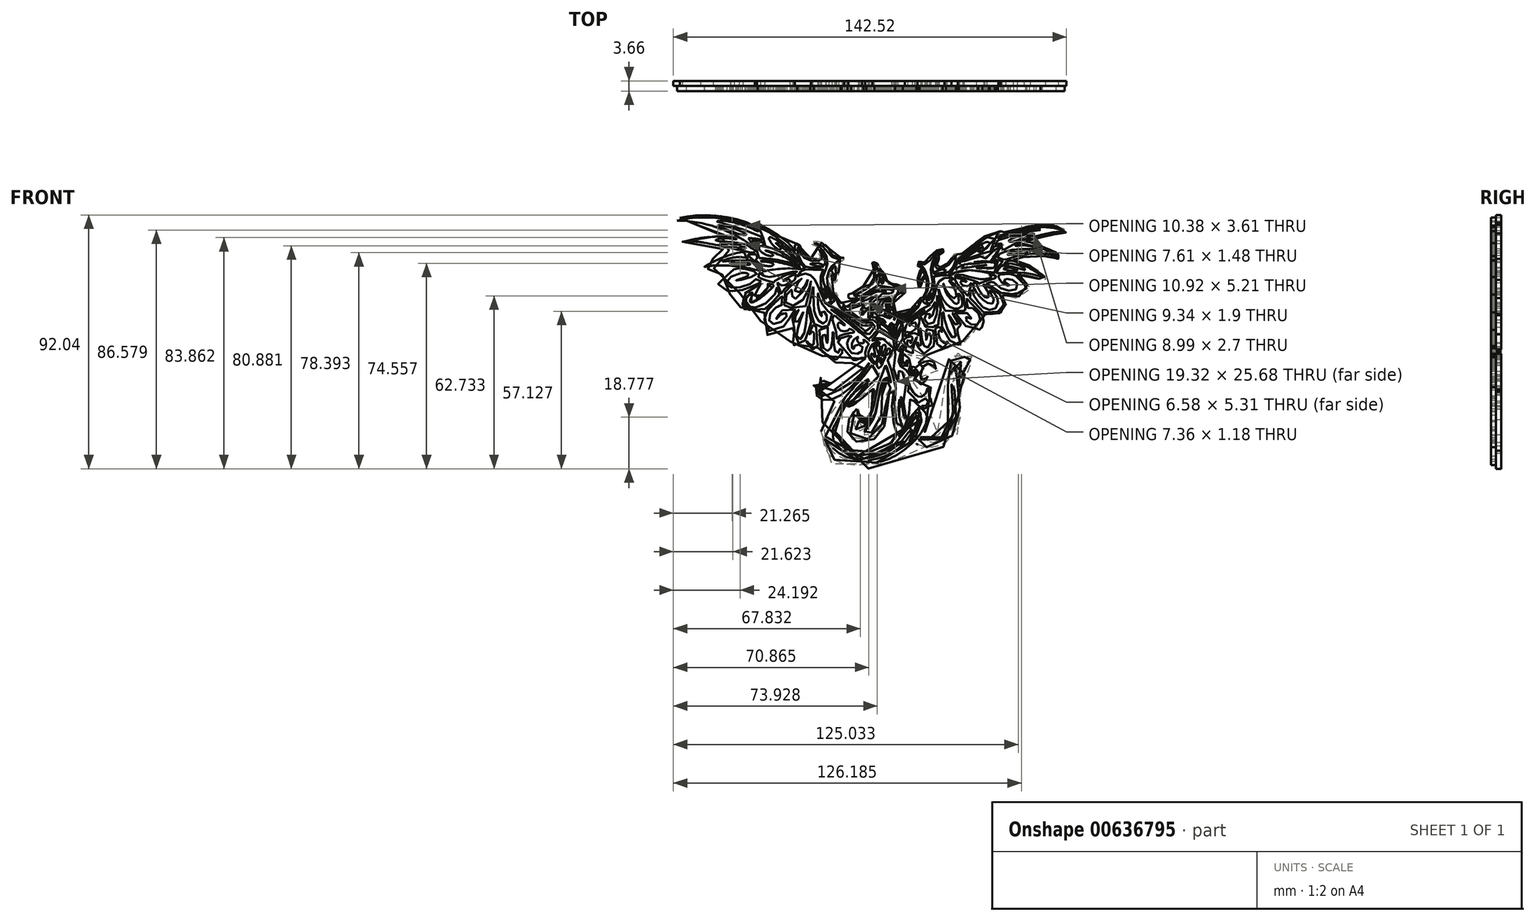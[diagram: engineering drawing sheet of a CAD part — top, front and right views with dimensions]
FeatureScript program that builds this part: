
annotation { "Feature Type Name" : "Feature", "Feature Type Description" : "" }
export const myFeature = defineFeature(function(context is Context, id is Id, definition is map)
    precondition{}
    {
        {
            var Q0;
            Q0=qCreatedBy(makeId("Front.planeOp"),FACE);
            var sketch = newSketch(context, id + "F0", { "sketchPlane" : qUnion([Q0])});
            skArc(sketch, "E0", {"start": v(-40.77, 53.62) * mm, "mid": v(-55.15, 57.82) * mm, "end": v(-70.1, 56.92) * mm});
            skArc(sketch, "E1", {"start": v(-40.6, 52.92) * mm, "mid": v(-40.59, 53.3) * mm, "end": v(-40.77, 53.62) * mm});
            skArc(sketch, "E2", {"start": v(-42.99, 47.81) * mm, "mid": v(-55.82, 54.53) * mm, "end": v(-70.1, 56.92) * mm});
            skArc(sketch, "E3", {"start": v(-42.99, 47.81) * mm, "mid": v(-43.46, 49.24) * mm, "end": v(-44.23, 50.52) * mm});
            skArc(sketch, "E4", {"start": v(-39.37, 49.9) * mm, "mid": v(-41.78, 50.38) * mm, "end": v(-44.23, 50.52) * mm});
            skArc(sketch, "E5", {"start": v(-39.37, 49.9) * mm, "mid": v(-39.28, 49.96) * mm, "end": v(-39.27, 50.07) * mm});
            skArc(sketch, "E6", {"start": v(-39.27, 50.07) * mm, "mid": v(-39.45, 50.65) * mm, "end": v(-39.76, 51.18) * mm});
            skArc(sketch, "E7", {"start": v(-39.76, 51.18) * mm, "mid": v(-47.54, 54.14) * mm, "end": v(-55.52, 56.51) * mm});
            skArc(sketch, "E8", {"start": v(-55.52, 56.73) * mm, "mid": v(-55.53, 56.62) * mm, "end": v(-55.52, 56.51) * mm});
            skArc(sketch, "E9", {"start": v(-50.72, 56.51) * mm, "mid": v(-53.1, 56.86) * mm, "end": v(-55.52, 56.73) * mm});
            skArc(sketch, "E10", {"start": v(-40.6, 52.92) * mm, "mid": v(-45.53, 55.07) * mm, "end": v(-50.72, 56.51) * mm});
            skSolve(sketch);
        }
        {
            var Q0;
            Q0=qCreatedBy(makeId("Front.planeOp"),FACE);
            var sketch = newSketch(context, id + "F1", { "sketchPlane" : qUnion([Q0])});
            skArc(sketch, "E11", {"start": v(-48.78, 52.4) * mm, "mid": v(-47, 51.89) * mm, "end": v(-45.15, 51.67) * mm});
            skArc(sketch, "E12", {"start": v(-45.15, 51.67) * mm, "mid": v(-45, 51.9) * mm, "end": v(-45.13, 52.16) * mm});
            skArc(sketch, "E13", {"start": v(-45.13, 52.16) * mm, "mid": v(-49.74, 54.12) * mm, "end": v(-54.62, 55.26) * mm});
            skArc(sketch, "E14", {"start": v(-54.62, 55.26) * mm, "mid": v(-55, 55.28) * mm, "end": v(-55.38, 55.16) * mm});
            skArc(sketch, "E15", {"start": v(-55.38, 55.16) * mm, "mid": v(-54.86, 54.8) * mm, "end": v(-54.27, 54.56) * mm});
            skArc(sketch, "E16", {"start": v(-54.27, 54.56) * mm, "mid": v(-51.53, 53.48) * mm, "end": v(-48.78, 52.4) * mm});
            skSolve(sketch);
        }
        {
            var Q0;
            Q0=makeQuery(id+"F0.imprint","IMPRINT",FACE,{"disambiguationData":[TD([[makeQuery(id+"F0.imprint","IMPRINT",EDGE,{"derivedFrom":sQuery(id+"F0.wireOp",EDGE,"E0")}),1.0]])]});
            var Q1;
            Q1=makeQuery(id+"F1.imprint","IMPRINT",FACE,{"disambiguationData":[TD([[makeQuery(id+"F1.imprint","IMPRINT",EDGE,{"derivedFrom":sQuery(id+"F1.wireOp",EDGE,"E11")}),1.0]])]});
            extrude(context, id + "F2", {"entities" : qUnion([Q0, Q1]), "depth" : 1.83 * mm, "offsetDistance" : 25.4 * mm});
        }
        {
            var Q0;
            Q0=makeQuery(id+"F1.imprint","IMPRINT",FACE,{"disambiguationData":[TD([[makeQuery(id+"F1.imprint","IMPRINT",EDGE,{"derivedFrom":sQuery(id+"F1.wireOp",EDGE,"E11")}),1.0]])]});
            extrude(context, id + "F3", {"entities" : qUnion([Q0]), "operationType" : NewBodyOperationType.REMOVE, "depth" : 5.46 * mm, "offsetDistance" : 25.4 * mm});
        }
        {
            var Q0;
            Q0=qCreatedBy(makeId("Front.planeOp"),FACE);
            var sketch = newSketch(context, id + "F4", { "sketchPlane" : qUnion([Q0])});
            skArc(sketch, "E17", {"start": v(-38.05, 47.64) * mm, "mid": v(-39.17, 51.49) * mm, "end": v(-40.89, 55.1) * mm});
            skArc(sketch, "E18", {"start": v(-26.6, 41.7) * mm, "mid": v(-32.02, 45.26) * mm, "end": v(-38.05, 47.64) * mm});
            skArc(sketch, "E19", {"start": v(-26.6, 41.7) * mm, "mid": v(-26.54, 41.8) * mm, "end": v(-26.6, 41.9) * mm});
            skArc(sketch, "E20", {"start": v(-26.6, 41.9) * mm, "mid": v(-30.13, 45.65) * mm, "end": v(-34.16, 48.86) * mm});
            skArc(sketch, "E21", {"start": v(-34.16, 48.86) * mm, "mid": v(-34.23, 48.76) * mm, "end": v(-34.2, 48.64) * mm});
            skArc(sketch, "E22", {"start": v(-32.64, 47.14) * mm, "mid": v(-33.36, 47.95) * mm, "end": v(-34.2, 48.64) * mm});
            skArc(sketch, "E23", {"start": v(-32.64, 46.38) * mm, "mid": v(-32.53, 46.76) * mm, "end": v(-32.64, 47.14) * mm});
            skArc(sketch, "E24", {"start": v(-33.49, 46.52) * mm, "mid": v(-33.08, 46.36) * mm, "end": v(-32.64, 46.38) * mm});
            skArc(sketch, "E25", {"start": v(-36.74, 50.34) * mm, "mid": v(-35.42, 48.17) * mm, "end": v(-33.49, 46.52) * mm});
            skArc(sketch, "E26", {"start": v(-36, 50.86) * mm, "mid": v(-36.54, 50.85) * mm, "end": v(-36.74, 50.34) * mm});
            skArc(sketch, "E27", {"start": v(-34.18, 49.92) * mm, "mid": v(-35.07, 50.42) * mm, "end": v(-36, 50.86) * mm});
            skArc(sketch, "E28", {"start": v(-25.33, 41.19) * mm, "mid": v(-29.35, 45.97) * mm, "end": v(-34.18, 49.92) * mm});
            skArc(sketch, "E29", {"start": v(-25.42, 40.9) * mm, "mid": v(-25.34, 41.03) * mm, "end": v(-25.33, 41.19) * mm});
            skArc(sketch, "E30", {"start": v(-26.8, 41.19) * mm, "mid": v(-26.13, 40.93) * mm, "end": v(-25.42, 40.9) * mm});
            skArc(sketch, "E31", {"start": v(-26.8, 41.19) * mm, "mid": v(-32.16, 44.18) * mm, "end": v(-37.97, 46.16) * mm});
            skArc(sketch, "E32", {"start": v(-37.97, 46.16) * mm, "mid": v(-38.03, 46.15) * mm, "end": v(-38.06, 46.1) * mm});
            skArc(sketch, "E33", {"start": v(-38.06, 46.1) * mm, "mid": v(-38.04, 46.03) * mm, "end": v(-37.97, 45.99) * mm});
            skArc(sketch, "E34", {"start": v(-36.61, 45.49) * mm, "mid": v(-37.28, 45.77) * mm, "end": v(-37.97, 45.99) * mm});
            skArc(sketch, "E35", {"start": v(-35.28, 44.44) * mm, "mid": v(-35.84, 45.1) * mm, "end": v(-36.61, 45.49) * mm});
            skArc(sketch, "E36", {"start": v(-35.31, 44.26) * mm, "mid": v(-35.26, 44.34) * mm, "end": v(-35.28, 44.44) * mm});
            skArc(sketch, "E37", {"start": v(-36.88, 44.26) * mm, "mid": v(-36.1, 44.12) * mm, "end": v(-35.31, 44.26) * mm});
            skArc(sketch, "E38", {"start": v(-40.41, 46.57) * mm, "mid": v(-38.87, 45.08) * mm, "end": v(-36.88, 44.26) * mm});
            skArc(sketch, "E39", {"start": v(-38.93, 47.66) * mm, "mid": v(-40, 47.57) * mm, "end": v(-40.41, 46.57) * mm});
            skArc(sketch, "E40", {"start": v(-38.93, 47.66) * mm, "mid": v(-38.85, 48.4) * mm, "end": v(-39.25, 49.04) * mm});
            skArc(sketch, "E41", {"start": v(-39.25, 49.04) * mm, "mid": v(-41.14, 49.54) * mm, "end": v(-43.07, 49.84) * mm});
            skArc(sketch, "E42", {"start": v(-40.41, 43.35) * mm, "mid": v(-41.47, 46.7) * mm, "end": v(-43.07, 49.84) * mm});
            skArc(sketch, "E43", {"start": v(-26.8, 40.9) * mm, "mid": v(-33.51, 42.63) * mm, "end": v(-40.41, 43.35) * mm});
            skArc(sketch, "E44", {"start": v(-25.65, 40.14) * mm, "mid": v(-26.14, 40.64) * mm, "end": v(-26.8, 40.9) * mm});
            skArc(sketch, "E45", {"start": v(-25.72, 39.85) * mm, "mid": v(-25.64, 39.98) * mm, "end": v(-25.65, 40.14) * mm});
            skArc(sketch, "E46", {"start": v(-27.02, 40.14) * mm, "mid": v(-26.38, 39.95) * mm, "end": v(-25.72, 39.85) * mm});
            skArc(sketch, "E47", {"start": v(-27.02, 40.14) * mm, "mid": v(-30.32, 41.12) * mm, "end": v(-33.67, 41.9) * mm});
            skArc(sketch, "E48", {"start": v(-33.67, 41.9) * mm, "mid": v(-36.75, 42.4) * mm, "end": v(-39.88, 42.32) * mm});
            skArc(sketch, "E49", {"start": v(-39.33, 42) * mm, "mid": v(-39.6, 42.18) * mm, "end": v(-39.88, 42.32) * mm});
            skArc(sketch, "E50", {"start": v(-37.02, 41.9) * mm, "mid": v(-38.17, 42.04) * mm, "end": v(-39.33, 42) * mm});
            skArc(sketch, "E51", {"start": v(-35.1, 41.14) * mm, "mid": v(-36, 41.65) * mm, "end": v(-37.02, 41.9) * mm});
            skArc(sketch, "E52", {"start": v(-35.93, 40.46) * mm, "mid": v(-35.4, 40.67) * mm, "end": v(-35.1, 41.14) * mm});
            skArc(sketch, "E53", {"start": v(-38.64, 40.64) * mm, "mid": v(-37.3, 40.45) * mm, "end": v(-35.93, 40.46) * mm});
            skArc(sketch, "E54", {"start": v(-41.35, 42.49) * mm, "mid": v(-40.15, 41.33) * mm, "end": v(-38.64, 40.64) * mm});
            skArc(sketch, "E55", {"start": v(-41.1, 43.17) * mm, "mid": v(-41.46, 42.91) * mm, "end": v(-41.35, 42.49) * mm});
            skArc(sketch, "E56", {"start": v(-41.1, 43.17) * mm, "mid": v(-41.06, 43.2) * mm, "end": v(-41.03, 43.23) * mm});
            skArc(sketch, "E57", {"start": v(-41.03, 43.23) * mm, "mid": v(-41.18, 43.99) * mm, "end": v(-41.53, 44.67) * mm});
            skArc(sketch, "E58", {"start": v(-41.53, 44.67) * mm, "mid": v(-42.78, 44.77) * mm, "end": v(-44.02, 44.67) * mm});
            skArc(sketch, "E59", {"start": v(-44.02, 44.67) * mm, "mid": v(-44.23, 44.57) * mm, "end": v(-44.38, 44.38) * mm});
            skArc(sketch, "E60", {"start": v(-38.75, 38.5) * mm, "mid": v(-41.42, 41.58) * mm, "end": v(-44.38, 44.38) * mm});
            skArc(sketch, "E61", {"start": v(-26.95, 39.5) * mm, "mid": v(-32.89, 39.43) * mm, "end": v(-38.75, 38.5) * mm});
            skArc(sketch, "E62", {"start": v(-24.8, 39.3) * mm, "mid": v(-25.87, 39.4) * mm, "end": v(-26.95, 39.5) * mm});
            skArc(sketch, "E63", {"start": v(-24.19, 39.5) * mm, "mid": v(-24.51, 39.46) * mm, "end": v(-24.8, 39.3) * mm});
            skArc(sketch, "E64", {"start": v(-24.19, 39.5) * mm, "mid": v(-23.87, 39.64) * mm, "end": v(-23.58, 39.83) * mm});
            skArc(sketch, "E65", {"start": v(-23.82, 39.92) * mm, "mid": v(-23.7, 39.86) * mm, "end": v(-23.58, 39.83) * mm});
            skArc(sketch, "E66", {"start": v(-26.4, 44.25) * mm, "mid": v(-25.49, 41.86) * mm, "end": v(-23.82, 39.92) * mm});
            skArc(sketch, "E67", {"start": v(-26.4, 44.25) * mm, "mid": v(-33.23, 50.24) * mm, "end": v(-40.89, 55.1) * mm});
            skSolve(sketch);
        }
        {
            var Q0;
            Q0=makeQuery(id+"F4.imprint","IMPRINT",FACE,{"disambiguationData":[TD([[makeQuery(id+"F4.imprint","IMPRINT",EDGE,{"derivedFrom":sQuery(id+"F4.wireOp",EDGE,"E17")}),-1.0]])]});
            extrude(context, id + "F5", {"entities" : qUnion([Q0]), "depth" : 1.83 * mm, "offsetDistance" : 25.4 * mm});
        }
        {
            var Q0;
            Q0=qCreatedBy(makeId("Front.planeOp"),FACE);
            var sketch = newSketch(context, id + "F6", { "sketchPlane" : qUnion([Q0])});
            skArc(sketch, "E68", {"start": v(-49.84, 50.91) * mm, "mid": v(-58.28, 50.99) * mm, "end": v(-66.62, 49.6) * mm});
            skArc(sketch, "E69", {"start": v(-48.6, 50.33) * mm, "mid": v(-49.21, 50.64) * mm, "end": v(-49.84, 50.91) * mm});
            skArc(sketch, "E70", {"start": v(-48.57, 50.12) * mm, "mid": v(-48.52, 50.24) * mm, "end": v(-48.6, 50.33) * mm});
            skArc(sketch, "E71", {"start": v(-49.67, 50.33) * mm, "mid": v(-49.13, 50.18) * mm, "end": v(-48.57, 50.12) * mm});
            skArc(sketch, "E72", {"start": v(-49.67, 50.33) * mm, "mid": v(-51.75, 50.52) * mm, "end": v(-53.83, 50.48) * mm});
            skArc(sketch, "E73", {"start": v(-53.83, 50.48) * mm, "mid": v(-55, 50.32) * mm, "end": v(-56.12, 49.87) * mm});
            skArc(sketch, "E74", {"start": v(-56.12, 49.87) * mm, "mid": v(-55.84, 49.73) * mm, "end": v(-55.54, 49.65) * mm});
            skArc(sketch, "E75", {"start": v(-55.54, 49.65) * mm, "mid": v(-54.6, 49.45) * mm, "end": v(-53.63, 49.31) * mm});
            skArc(sketch, "E76", {"start": v(-45.04, 48.31) * mm, "mid": v(-49.31, 49) * mm, "end": v(-53.63, 49.31) * mm});
            skArc(sketch, "E77", {"start": v(-45.04, 48.31) * mm, "mid": v(-43.73, 47.36) * mm, "end": v(-42.36, 46.5) * mm});
            skArc(sketch, "E78", {"start": v(-41.82, 45.43) * mm, "mid": v(-41.95, 46.03) * mm, "end": v(-42.36, 46.5) * mm});
            skArc(sketch, "E79", {"start": v(-44, 45.43) * mm, "mid": v(-42.91, 45.36) * mm, "end": v(-41.82, 45.43) * mm});
            skArc(sketch, "E80", {"start": v(-44, 45.43) * mm, "mid": v(-52.12, 47.34) * mm, "end": v(-60.3, 48.96) * mm});
            skArc(sketch, "E81", {"start": v(-60.3, 48.96) * mm, "mid": v(-63.45, 49.4) * mm, "end": v(-66.62, 49.6) * mm});
            skSolve(sketch);
        }
        {
            var Q0;
            Q0=qCreatedBy(makeId("Front.planeOp"),FACE);
            var sketch = newSketch(context, id + "F7", { "sketchPlane" : qUnion([Q0])});
            skArc(sketch, "E82", {"start": v(-54.5, 48.54) * mm, "mid": v(-54.44, 48.45) * mm, "end": v(-54.33, 48.4) * mm});
            skArc(sketch, "E83", {"start": v(-54.17, 48.72) * mm, "mid": v(-54.37, 48.7) * mm, "end": v(-54.5, 48.54) * mm});
            skArc(sketch, "E84", {"start": v(-45.2, 47.13) * mm, "mid": v(-49.6, 48.36) * mm, "end": v(-54.17, 48.72) * mm});
            skArc(sketch, "E85", {"start": v(-45.2, 46.91) * mm, "mid": v(-45.16, 47.02) * mm, "end": v(-45.2, 47.13) * mm});
            skArc(sketch, "E86", {"start": v(-45.74, 46.83) * mm, "mid": v(-45.46, 46.85) * mm, "end": v(-45.2, 46.91) * mm});
            skArc(sketch, "E87", {"start": v(-54.33, 48.4) * mm, "mid": v(-50.08, 47.36) * mm, "end": v(-45.74, 46.83) * mm});
            skSolve(sketch);
        }
        {
            var Q0;
            Q0=makeQuery(id+"F6.imprint","IMPRINT",FACE,{"disambiguationData":[TD([[makeQuery(id+"F6.imprint","IMPRINT",EDGE,{"derivedFrom":sQuery(id+"F6.wireOp",EDGE,"E68")}),1.0]])]});
            extrude(context, id + "F8", {"entities" : qUnion([Q0]), "depth" : 1.83 * mm, "offsetDistance" : 25.4 * mm});
        }
        {
            var Q0;
            Q0=makeQuery(id+"F7.imprint","IMPRINT",FACE,{"disambiguationData":[TD([[makeQuery(id+"F7.imprint","IMPRINT",EDGE,{"derivedFrom":sQuery(id+"F7.wireOp",EDGE,"E82")}),1.0]])]});
            extrude(context, id + "F9", {"entities" : qUnion([Q0]), "operationType" : NewBodyOperationType.REMOVE, "depth" : 12.2 * mm, "offsetDistance" : 25.4 * mm});
        }
        {
            var Q0;
            Q0=qCreatedBy(makeId("Front.planeOp"),FACE);
            var sketch = newSketch(context, id + "F10", { "sketchPlane" : qUnion([Q0])});
            skArc(sketch, "E88", {"start": v(-45.43, 44.47) * mm, "mid": v(-44.95, 43.94) * mm, "end": v(-44.4, 43.47) * mm});
            skArc(sketch, "E89", {"start": v(-45.43, 45.01) * mm, "mid": v(-45.47, 44.74) * mm, "end": v(-45.43, 44.47) * mm});
            skArc(sketch, "E90", {"start": v(-45.43, 45.01) * mm, "mid": v(-45.95, 45.32) * mm, "end": v(-46.5, 45.54) * mm});
            skArc(sketch, "E91", {"start": v(-46.5, 45.54) * mm, "mid": v(-53.55, 43.56) * mm, "end": v(-60.08, 40.25) * mm});
            skArc(sketch, "E92", {"start": v(-60.08, 40.25) * mm, "mid": v(-60.1, 40.19) * mm, "end": v(-60.05, 40.16) * mm});
            skArc(sketch, "E93", {"start": v(-55.05, 40.67) * mm, "mid": v(-57.56, 40.58) * mm, "end": v(-60.05, 40.16) * mm});
            skArc(sketch, "E94", {"start": v(-40, 38.68) * mm, "mid": v(-47.45, 40.24) * mm, "end": v(-55.05, 40.67) * mm});
            skArc(sketch, "E95", {"start": v(-40, 38.68) * mm, "mid": v(-39.91, 38.72) * mm, "end": v(-39.86, 38.8) * mm});
            skArc(sketch, "E96", {"start": v(-39.86, 38.8) * mm, "mid": v(-41.59, 40.7) * mm, "end": v(-43.42, 42.5) * mm});
            skArc(sketch, "E97", {"start": v(-53.36, 42.4) * mm, "mid": v(-53.5, 42.28) * mm, "end": v(-53.43, 42.1) * mm});
            skArc(sketch, "E98", {"start": v(-44.47, 43.28) * mm, "mid": v(-49, 43.62) * mm, "end": v(-53.36, 42.4) * mm});
            skArc(sketch, "E99", {"start": v(-44.47, 43.28) * mm, "mid": v(-44.38, 43.35) * mm, "end": v(-44.4, 43.47) * mm});
            skArc(sketch, "E100", {"start": v(-48.28, 42.4) * mm, "mid": v(-50.86, 42.34) * mm, "end": v(-53.43, 42.1) * mm});
            skArc(sketch, "E101", {"start": v(-43.42, 42.5) * mm, "mid": v(-45.85, 42.48) * mm, "end": v(-48.28, 42.4) * mm});
            skSolve(sketch);
        }
        {
            var Q0;
            Q0=makeQuery(id+"F10.imprint","IMPRINT",FACE,{"disambiguationData":[TD([[makeQuery(id+"F10.imprint","IMPRINT",EDGE,{"derivedFrom":sQuery(id+"F10.wireOp",EDGE,"E88")}),-1.0]])]});
            extrude(context, id + "F11", {"entities" : qUnion([Q0]), "depth" : 1.83 * mm, "offsetDistance" : 25.4 * mm});
        }
        {
            var Q0;
            Q0=qCreatedBy(makeId("Front.planeOp"),FACE);
            var sketch = newSketch(context, id + "F12", { "sketchPlane" : qUnion([Q0])});
            skArc(sketch, "E102", {"start": v(-50.87, 41.4) * mm, "mid": v(-50.6, 41.3) * mm, "end": v(-50.33, 41.26) * mm});
            skArc(sketch, "E103", {"start": v(-50.87, 41.62) * mm, "mid": v(-50.94, 41.51) * mm, "end": v(-50.87, 41.4) * mm});
            skArc(sketch, "E104", {"start": v(-43.7, 41.4) * mm, "mid": v(-47.27, 42.05) * mm, "end": v(-50.87, 41.62) * mm});
            skArc(sketch, "E105", {"start": v(-43.7, 40.96) * mm, "mid": v(-43.58, 41.18) * mm, "end": v(-43.7, 41.4) * mm});
            skArc(sketch, "E106", {"start": v(-50.33, 41.26) * mm, "mid": v(-47.02, 40.89) * mm, "end": v(-43.7, 40.96) * mm});
            skSolve(sketch);
        }
        {
            var Q0;
            Q0 = qSketchRegion(id + "F12", true);
            extrude(context, id + "F13", {"entities" : qUnion([Q0]), "operationType" : NewBodyOperationType.REMOVE, "depth" : 25.4 * mm, "offsetDistance" : 25.4 * mm});
        }
        {
            var Q0;
            Q0=qCreatedBy(makeId("Front.planeOp"),FACE);
            var sketch = newSketch(context, id + "F14", { "sketchPlane" : qUnion([Q0])});
            skArc(sketch, "E107", {"start": v(-48.7, 35.2) * mm, "mid": v(-48.64, 35.18) * mm, "end": v(-48.57, 35.2) * mm});
            skArc(sketch, "E108", {"start": v(-48.7, 35.32) * mm, "mid": v(-48.72, 35.26) * mm, "end": v(-48.7, 35.2) * mm});
            skArc(sketch, "E109", {"start": v(-48.7, 35.32) * mm, "mid": v(-48.24, 35.44) * mm, "end": v(-47.78, 35.58) * mm});
            skFitSpline(sketch, "E110", {"points": [v(-47.78, 35.58) * mm, v(-44.29, 37.27) * mm, v(-44.4, 37.7) * mm, v(-44.4, 37.67) * mm, v(-44.4, 37.68) * mm], "startDerivative": vector(7.46, 2.33) * mm, "endDerivative": vector(0.28, 0.45) * mm});
            skArc(sketch, "E111", {"start": v(-44.4, 37.68) * mm, "mid": v(-45.74, 38) * mm, "end": v(-47.11, 37.88) * mm});
            skFitSpline(sketch, "E112", {"points": [v(-47.11, 37.88) * mm, v(-50.57, 36.51) * mm, v(-51.69, 35.46) * mm, v(-51.95, 34.74) * mm, v(-51.96, 33.96) * mm, v(-51.61, 33.32) * mm, v(-51.11, 32.92) * mm, v(-50.54, 32.69) * mm, v(-48.43, 32.65) * mm, v(-45.08, 33.38) * mm, v(-41.98, 35.07) * mm, v(-41.38, 35.78) * mm, v(-41, 35.53) * mm, v(-39.63, 34.88) * mm, v(-39.67, 34.77) * mm, v(-39.93, 34.52) * mm, v(-40.7, 34.13) * mm, v(-42.68, 33.16) * mm, v(-45.8, 31.94) * mm, v(-49.7, 31.38) * mm, v(-51.04, 31.18) * mm, v(-51.23, 31.16) * mm, v(-55.08, 33.82) * mm, v(-55.12, 34.1) * mm, v(-53.64, 35.58) * mm, v(-49.26, 39.54) * mm, v(-49.16, 39.59) * mm, v(-47.93, 39.6) * mm, v(-45.95, 39.44) * mm, v(-44.31, 39.2) * mm, v(-41.57, 38.5) * mm, v(-41.23, 38.42) * mm, v(-41.2, 37.5) * mm, v(-41.22, 37.38) * mm, v(-44.02, 36.24) * mm, v(-47.05, 35.45) * mm, v(-48.18, 35.24) * mm, v(-48.57, 35.2) * mm], "startDerivative": vector(-88.5, -28.85) * mm, "endDerivative": vector(-24.4, -1.68) * mm});
            skSolve(sketch);
        }
        {
            var Q0;
            Q0 = qSketchRegion(id + "F14", true);
            extrude(context, id + "F15", {"entities" : qUnion([Q0]), "depth" : 1.83 * mm, "offsetDistance" : 25.4 * mm});
        }
        {
            var Q0;
            Q0=qCreatedBy(makeId("Front.planeOp"),FACE);
            var sketch = newSketch(context, id + "F16", { "sketchPlane" : qUnion([Q0])});
            skFitSpline(sketch, "E113", {"points": [v(-38.89, 37.85) * mm, v(-39.35, 37.62) * mm, v(-39.47, 37.4) * mm, v(-39.34, 37.2) * mm, v(-38.84, 36.95) * mm, v(-37.39, 36.55) * mm, v(-35.11, 36.71) * mm, v(-27.73, 38.42) * mm, v(-26.95, 38.5) * mm, v(-26.59, 38.5) * mm, v(-26.58, 38.44) * mm, v(-27.4, 38.17) * mm, v(-29.43, 37.54) * mm, v(-30.77, 37.1) * mm, v(-32.37, 36.3) * mm, v(-34.38, 35.16) * mm, v(-34.94, 34.68) * mm, v(-35.02, 34.56) * mm, v(-35.02, 34.54) * mm, v(-37.35, 35.15) * mm, v(-39.65, 35.95) * mm, v(-40.42, 36.37) * mm, v(-40.54, 36.46) * mm, v(-40.48, 37.04) * mm, v(-40.2, 37.9) * mm, v(-40.14, 37.92) * mm, v(-38.89, 37.85) * mm]});
            skSolve(sketch);
        }
        {
            var Q0;
            Q0 = qSketchRegion(id + "F16", true);
            extrude(context, id + "F17", {"entities" : qUnion([Q0]), "depth" : 1.83 * mm, "offsetDistance" : 25.4 * mm});
        }
        {
            var Q0;
            Q0=qCreatedBy(makeId("Front.planeOp"),FACE);
            var sketch = newSketch(context, id + "F18", { "sketchPlane" : qUnion([Q0])});
            skFitSpline(sketch, "E114", {"points": [v(-37.05, 34) * mm, v(-35.03, 33.59) * mm, v(-34.99, 33.38) * mm, v(-35.23, 33.01) * mm, v(-37.45, 30.91) * mm, v(-39.33, 29.33) * mm, v(-41.86, 27.66) * mm, v(-42.67, 27.26) * mm, v(-43.28, 27.22) * mm, v(-43.5, 27.37) * mm, v(-43.62, 27.76) * mm, v(-43.53, 28.21) * mm, v(-43.05, 29.24) * mm, v(-42.64, 30.16) * mm, v(-42.61, 30.64) * mm, v(-42.72, 30.83) * mm, v(-43, 30.86) * mm, v(-43.57, 30.65) * mm, v(-44.27, 29.9) * mm, v(-44.82, 29.06) * mm, v(-45.2, 28.19) * mm, v(-45.3, 26.85) * mm, v(-45.24, 26.23) * mm, v(-44.64, 25.69) * mm, v(-43.48, 25.49) * mm, v(-42.32, 25.43) * mm, v(-40.6, 25.59) * mm, v(-39.3, 26.11) * mm, v(-37.42, 27.29) * mm, v(-35.58, 29) * mm, v(-34.3, 30.72) * mm, v(-34, 31.6) * mm, v(-33.93, 32.14) * mm, v(-33.91, 32.52) * mm, v(-33.88, 32.67) * mm, v(-33.7, 32.68) * mm, v(-33.67, 32.3) * mm, v(-33.13, 30.49) * mm, v(-32.95, 30.2) * mm, v(-33.04, 29.8) * mm, v(-34.06, 28.77) * mm, v(-35.82, 27.01) * mm, v(-37.4, 25.66) * mm, v(-38.23, 24.86) * mm, v(-38.36, 24.78) * mm, v(-41.4, 24.83) * mm, v(-45.28, 24.41) * mm, v(-45.5, 24.56) * mm, v(-45.75, 25.1) * mm, v(-46.36, 26.59) * mm, v(-46.23, 27.21) * mm, v(-45.05, 31.22) * mm, v(-44.69, 31.4) * mm, v(-39.04, 34.23) * mm, v(-39.03, 34.03) * mm, v(-39.68, 33.48) * mm, v(-40.65, 32.28) * mm, v(-41.43, 31.1) * mm, v(-41.83, 30.2) * mm, v(-41.96, 29.8) * mm, v(-41.9, 29.23) * mm, v(-41.64, 29.03) * mm, v(-41.1, 29.07) * mm, v(-39.93, 29.79) * mm, v(-38.6, 30.88) * mm, v(-37.4, 32.27) * mm, v(-37.14, 32.7) * mm, v(-37.1, 33.09) * mm, v(-37.13, 33.43) * mm, v(-37.2, 33.78) * mm, v(-37.21, 33.93) * mm, v(-37.05, 34) * mm]});
            skSolve(sketch);
        }
        {
            var Q0;
            Q0 = qSketchRegion(id + "F18", true);
            extrude(context, id + "F19", {"entities" : qUnion([Q0]), "depth" : 1.83 * mm, "offsetDistance" : 25.4 * mm});
        }
        {
            var Q0;
            Q0=qCreatedBy(makeId("Front.planeOp"),FACE);
            var sketch = newSketch(context, id + "F20", { "sketchPlane" : qUnion([Q0])});
            skFitSpline(sketch, "E115", {"points": [v(-33.68, 34.55) * mm, v(-33.38, 34.27) * mm, v(-33.02, 33.77) * mm, v(-32.31, 33.41) * mm, v(-31.52, 33.34) * mm, v(-30.11, 33.91) * mm, v(-29.43, 34.46) * mm, v(-29.03, 35.15) * mm, v(-29.15, 35.62) * mm, v(-29.75, 35.69) * mm, v(-30.86, 35.42) * mm, v(-31.25, 35.16) * mm, v(-31.56, 34.99) * mm, v(-31.65, 34.99) * mm, v(-31.69, 35.2) * mm, v(-31.31, 35.47) * mm, v(-30.13, 36.17) * mm, v(-27.53, 37.32) * mm, v(-26.93, 37.53) * mm, v(-26.81, 37.46) * mm, v(-26.89, 37.36) * mm, v(-27.07, 36.84) * mm, v(-27.14, 36.47) * mm, v(-27.06, 35.9) * mm, v(-27.36, 35.55) * mm, v(-28.87, 34.23) * mm, v(-30.11, 33.08) * mm, v(-31.57, 31.5) * mm, v(-32.17, 30.6) * mm, v(-32.33, 30.4) * mm, v(-32.41, 30.44) * mm, v(-32.4, 30.63) * mm, v(-33.46, 33.38) * mm, v(-33.72, 34.17) * mm, v(-33.76, 34.43) * mm, v(-33.68, 34.55) * mm]});
            skSolve(sketch);
        }
        {
            var Q0;
            Q0 = qSketchRegion(id + "F20", true);
            extrude(context, id + "F21", {"entities" : qUnion([Q0]), "depth" : 1.83 * mm, "offsetDistance" : 25.4 * mm});
        }
        {
            var Q0;
            Q0=qCreatedBy(makeId("Front.planeOp"),FACE);
            var sketch = newSketch(context, id + "F22", { "sketchPlane" : qUnion([Q0])});
            skFitSpline(sketch, "E116", {"points": [v(-22.68, 35.58) * mm, v(-22.56, 35.69) * mm, v(-22.54, 35.37) * mm, v(-22.74, 34.55) * mm, v(-23.33, 33.16) * mm, v(-24.09, 31.83) * mm, v(-25.43, 30.2) * mm, v(-26.5, 29.12) * mm, v(-27.6, 28.37) * mm, v(-28.51, 28.4) * mm, v(-28.42, 29.12) * mm, v(-28.2, 30.63) * mm, v(-28.2, 31.6) * mm, v(-28.59, 31.88) * mm, v(-29.7, 31.48) * mm, v(-30.4, 30.38) * mm, v(-30.69, 29.19) * mm, v(-30.8, 28.05) * mm, v(-30.56, 27.03) * mm, v(-29.46, 26.17) * mm, v(-27.83, 26.1) * mm, v(-25.4, 27.32) * mm, v(-23.35, 29.84) * mm, v(-22, 32.77) * mm, v(-21.74, 34.33) * mm, v(-21.66, 34.88) * mm, v(-21.55, 34.88) * mm, v(-21.52, 34) * mm, v(-21.9, 31.87) * mm, v(-23.5, 26) * mm, v(-23.5, 25.96) * mm, v(-25.24, 25.84) * mm, v(-30.72, 25.2) * mm, v(-31.07, 25.46) * mm, v(-31.18, 26.72) * mm, v(-31.07, 30.88) * mm, v(-30.97, 31) * mm, v(-30.2, 31.92) * mm, v(-28.8, 33.23) * mm, v(-25.52, 35.6) * mm, v(-24.83, 35.86) * mm, v(-24.74, 35.69) * mm, v(-25.28, 35.34) * mm, v(-26.4, 34.25) * mm, v(-27.23, 32.84) * mm, v(-27.42, 31.49) * mm, v(-27.18, 30.66) * mm, v(-26.37, 30.66) * mm, v(-25.45, 31.21) * mm, v(-24.16, 32.63) * mm, v(-23.36, 33.9) * mm, v(-22.82, 34.95) * mm, v(-22.75, 35.36) * mm, v(-22.68, 35.58) * mm]});
            skSolve(sketch);
        }
        {
            var Q0;
            Q0=makeQuery(id+"F22.imprint","IMPRINT",FACE,{"disambiguationData":[TD([[makeQuery(id+"F22.imprint","IMPRINT",EDGE,{"derivedFrom":sQuery(id+"F22.wireOp",EDGE,"E116")}),-1.0]])]});
            extrude(context, id + "F23", {"entities" : qUnion([Q0]), "depth" : 1.83 * mm, "offsetDistance" : 25.4 * mm});
        }
        {
            var Q0;
            Q0=qCreatedBy(makeId("Front.planeOp"),FACE);
            var sketch = newSketch(context, id + "F24", { "sketchPlane" : qUnion([Q0])});
            skFitSpline(sketch, "E117", {"points": [v(-31.92, 24.4) * mm, v(-27.33, 24.7) * mm, v(-27.31, 24.6) * mm, v(-27.89, 23.67) * mm, v(-31.09, 18.91) * mm, v(-31.43, 18.52) * mm, v(-31.95, 18.41) * mm, v(-33.82, 17.8) * mm, v(-35.26, 17.33) * mm, v(-36.86, 16.8) * mm, v(-36.87, 16.8) * mm, v(-37.34, 18.3) * mm, v(-37.89, 19.88) * mm, v(-38.35, 20.84) * mm, v(-38.45, 21.22) * mm, v(-38.28, 21.85) * mm, v(-37.2, 24.77) * mm, v(-37.16, 24.83) * mm, v(-33.76, 27.88) * mm, v(-32.88, 28.78) * mm, v(-32.34, 29.44) * mm, v(-32.17, 29.62) * mm, v(-31.94, 29.68) * mm, v(-31.9, 29.56) * mm, v(-32.03, 26.42) * mm, v(-32.03, 26.34) * mm, v(-32.7, 26.3) * mm, v(-33.48, 25.92) * mm, v(-34.53, 25.25) * mm, v(-35.93, 23.87) * mm, v(-36.76, 22.3) * mm, v(-36.73, 20.81) * mm, v(-36.34, 20.04) * mm, v(-35.68, 19.57) * mm, v(-34.41, 19.52) * mm, v(-32.71, 20.09) * mm, v(-31.1, 21.17) * mm, v(-30.4, 22.1) * mm, v(-30.2, 22.68) * mm, v(-30.24, 23.14) * mm, v(-30.56, 23.37) * mm, v(-31.16, 23.36) * mm, v(-31.96, 23.12) * mm, v(-32.89, 22.57) * mm, v(-33.72, 21.74) * mm, v(-34.12, 21.26) * mm, v(-34.16, 21.3) * mm, v(-34.17, 21.5) * mm, v(-33.88, 21.9) * mm, v(-32.13, 24.11) * mm, v(-31.98, 24.3) * mm, v(-31.95, 24.36) * mm, v(-31.94, 24.37) * mm, v(-31.93, 24.39) * mm, v(-31.92, 24.39) * mm, v(-31.92, 24.4) * mm, v(-31.92, 24.4) * mm, v(-31.92, 24.4) * mm]});
            skSolve(sketch);
        }
        {
            var Q0;
            Q0=makeQuery(id+"F24.imprint","IMPRINT",FACE,{"disambiguationData":[TD([[makeQuery(id+"F24.imprint","IMPRINT",EDGE,{"derivedFrom":sQuery(id+"F24.wireOp",EDGE,"E117")}),-1.0]])]});
            extrude(context, id + "F25", {"entities" : qUnion([Q0]), "depth" : 1.83 * mm, "offsetDistance" : 25.4 * mm});
        }
        {
            var Q0;
            Q0=qCreatedBy(makeId("Front.planeOp"),FACE);
            var sketch = newSketch(context, id + "F26", { "sketchPlane" : qUnion([Q0])});
            skFitSpline(sketch, "E118", {"points": [v(-20.63, 32.94) * mm, v(-20.64, 30.1) * mm, v(-20.57, 26.68) * mm, v(-20.33, 24.05) * mm, v(-19.88, 22.65) * mm, v(-19.44, 21.58) * mm, v(-18.5, 20.21) * mm, v(-17.21, 19.57) * mm, v(-16.26, 20.12) * mm, v(-15.78, 20.97) * mm, v(-15.76, 22.11) * mm, v(-16.2, 23.22) * mm, v(-16.7, 23.91) * mm, v(-17.4, 24.13) * mm, v(-17.82, 23.62) * mm, v(-17.83, 22.92) * mm, v(-17.64, 22.2) * mm, v(-17.66, 21.94) * mm, v(-17.85, 22.13) * mm, v(-18.3, 23.29) * mm, v(-18.64, 24.33) * mm, v(-18.85, 25.26) * mm, v(-19.07, 27.83) * mm, v(-19.1, 29.68) * mm, v(-19.15, 30.44) * mm, v(-18.93, 30.54) * mm, v(-18.78, 29.9) * mm, v(-18.12, 27.8) * mm, v(-16.8, 25.7) * mm, v(-14.6, 23.4) * mm, v(-14.01, 23.01) * mm, v(-14.01, 22.8) * mm, v(-14.36, 21.6) * mm, v(-15.38, 18.95) * mm, v(-15.43, 18.83) * mm, v(-17.68, 18.27) * mm], "startDerivative": vector(-0.75, -62.98) * mm, "endDerivative": vector(-78.97, -16.88) * mm});
            skFitSpline(sketch, "E119", {"points": [v(-17.68, 18.27) * mm, v(-20.25, 19.49) * mm, v(-20.4, 19.59) * mm, v(-21.64, 24.11) * mm, v(-21.9, 25.28) * mm, v(-22.28, 26.1) * mm, v(-22.15, 26.6) * mm, v(-21.94, 27.3) * mm, v(-21.44, 29.8) * mm, v(-21.17, 30.98) * mm, v(-20.8, 32.68) * mm, v(-20.72, 32.85) * mm, v(-20.63, 32.94) * mm], "startDerivative": vector(-25.53, 12.8) * mm, "endDerivative": vector(3.47, 3.11) * mm});
            skSolve(sketch);
        }
        {
            var Q0;
            Q0 = qSketchRegion(id + "F26", true);
            extrude(context, id + "F27", {"entities" : qUnion([Q0]), "depth" : 1.83 * mm, "offsetDistance" : 25.4 * mm});
        }
        {
            var Q0;
            Q0=qCreatedBy(makeId("Front.planeOp"),FACE);
            var sketch = newSketch(context, id + "F28", { "sketchPlane" : qUnion([Q0])});
            skFitSpline(sketch, "E120", {"points": [v(-22.63, 25.6) * mm, v(-21.41, 20.15) * mm, v(-21.4, 20) * mm, v(-21.92, 18.34) * mm, v(-23.65, 13.63) * mm, v(-23.72, 13.46) * mm, v(-27.31, 11.9) * mm, v(-28.17, 11.52) * mm, v(-28.22, 11.64) * mm, v(-28.05, 12.82) * mm, v(-27.67, 16.25) * mm, v(-27.4, 18.69) * mm, v(-27.5, 18.87) * mm, v(-28.34, 20.36) * mm, v(-28.58, 20.95) * mm, v(-28.47, 21.15) * mm, v(-27.59, 22.44) * mm, v(-26.99, 23.47) * mm, v(-26.45, 24.35) * mm, v(-26.12, 24.74) * mm, v(-25.96, 24.74) * mm, v(-26.14, 24.47) * mm, v(-26.75, 23.3) * mm, v(-27.25, 22.18) * mm, v(-27.52, 21.08) * mm, v(-27.54, 20.51) * mm, v(-27.09, 19.9) * mm, v(-26.55, 19.95) * mm, v(-26.16, 20.38) * mm, v(-25.31, 21.82) * mm, v(-24.7, 23.15) * mm, v(-24.38, 23.9) * mm, v(-24.28, 24.02) * mm, v(-24.23, 24) * mm, v(-24.4, 23.36) * mm, v(-25.12, 21.54) * mm, v(-25.57, 20.32) * mm, v(-26.2, 18.37) * mm, v(-26.62, 16.26) * mm, v(-26.72, 15.24) * mm, v(-26.48, 14.36) * mm, v(-25.77, 13.93) * mm, v(-24.89, 14.2) * mm, v(-24.13, 15.54) * mm, v(-23.75, 17.07) * mm, v(-23.28, 20.25) * mm, v(-23.02, 23.37) * mm, v(-22.85, 25.38) * mm, v(-22.8, 25.53) * mm, v(-22.72, 25.57) * mm, v(-22.63, 25.6) * mm]});
            skSolve(sketch);
        }
        {
            var Q0;
            Q0 = qSketchRegion(id + "F28", true);
            extrude(context, id + "F29", {"entities" : qUnion([Q0]), "depth" : 1.83 * mm, "offsetDistance" : 25.4 * mm});
        }
        {
            var Q0;
            Q0=qCreatedBy(makeId("Front.planeOp"),FACE);
            var sketch = newSketch(context, id + "F30", { "sketchPlane" : qUnion([Q0])});
            skFitSpline(sketch, "E121", {"points": [v(-22.12, 15.97) * mm, v(-20.97, 18.87) * mm, v(-20.91, 18.93) * mm, v(-20.77, 18.91) * mm, v(-19.95, 18.48) * mm, v(-19.66, 18.28) * mm, v(-19.61, 17.84) * mm, v(-19.08, 11.93) * mm, v(-19.08, 11.74) * mm, v(-21.02, 10.15) * mm, v(-21.1, 10.13) * mm], "startDerivative": vector(8.04, 21.24) * mm, "endDerivative": vector(-1.36, 0.34) * mm});
            skFitSpline(sketch, "E122", {"points": [v(-21.09, 10.12) * mm, v(-23.07, 12.76) * mm, v(-23.13, 12.85) * mm, v(-23.15, 12.95) * mm], "startDerivative": vector(-3.65, 4.84) * mm, "endDerivative": vector(-0.15, 0.86) * mm});
            skFitSpline(sketch, "E123", {"points": [v(-23.15, 12.95) * mm, v(-23.15, 13) * mm, v(-23.1, 13.09) * mm, v(-22.94, 13.1) * mm, v(-22.63, 12.8) * mm, v(-21.94, 12.1) * mm, v(-21.19, 11.84) * mm, v(-20.63, 12.1) * mm, v(-20.5, 12.75) * mm, v(-20.44, 15) * mm, v(-20.42, 15.92) * mm, v(-20.73, 16.46) * mm, v(-21.09, 16.62) * mm, v(-21.47, 16.56) * mm, v(-21.67, 16.27) * mm, v(-21.86, 15.82) * mm, v(-21.98, 15.72) * mm, v(-22.08, 15.72) * mm, v(-22.14, 15.79) * mm, v(-22.15, 15.86) * mm, v(-22.12, 15.97) * mm], "startDerivative": vector(-0.37, 2.85) * mm, "endDerivative": vector(1.8, 4.94) * mm});
            skSolve(sketch);
        }
        {
            var Q0;
            Q0 = qSketchRegion(id + "F30", true);
            extrude(context, id + "F31", {"entities" : qUnion([Q0]), "depth" : 1.83 * mm, "offsetDistance" : 25.4 * mm});
        }
        {
            var Q0;
            Q0=qCreatedBy(makeId("Front.planeOp"),FACE);
            var sketch = newSketch(context, id + "F32", { "sketchPlane" : qUnion([Q0])});
            skFitSpline(sketch, "E124", {"points": [v(-15.5, 18.29) * mm, v(-15.62, 12.65) * mm, v(-15.75, 12.48) * mm], "startDerivative": vector(0.11, -9.1) * mm, "endDerivative": vector(-0.81, -0.6) * mm});
            skFitSpline(sketch, "E125", {"points": [v(-15.75, 12.48) * mm, v(-15.8, 12.48) * mm, v(-15.9, 12.51) * mm, v(-15.93, 12.72) * mm, v(-15.92, 12.93) * mm, v(-16, 14.55) * mm, v(-16.19, 15.23) * mm, v(-16.53, 15.65) * mm, v(-16.82, 15.8) * mm, v(-17.23, 15.53) * mm, v(-17.43, 14.92) * mm, v(-17.47, 13.54) * mm, v(-17.45, 12.12) * mm, v(-16.96, 10.65) * mm, v(-16.22, 9.84) * mm, v(-15.55, 9.67) * mm, v(-15, 9.8) * mm, v(-14.4, 10.47) * mm, v(-13.95, 12.02) * mm, v(-13.8, 13.59) * mm, v(-13.65, 16.46) * mm, v(-13.63, 16.66) * mm, v(-13.57, 16.78) * mm, v(-13.36, 16.74) * mm, v(-13.31, 16.4) * mm, v(-13.31, 13.18) * mm, v(-13.06, 10.28) * mm, v(-12.72, 9.44) * mm, v(-12.31, 8.97) * mm, v(-11.69, 8.96) * mm, v(-11.2, 9.68) * mm, v(-11.07, 10.1) * mm, v(-11.07, 10.42) * mm, v(-11.02, 10.58) * mm, v(-10.84, 10.6) * mm, v(-10.58, 10.23) * mm, v(-9.71, 9.38) * mm, v(-9.67, 9.23) * mm, v(-9.93, 9.1) * mm, v(-11, 7.93) * mm, v(-11.51, 7.3) * mm, v(-11.84, 6.84) * mm, v(-12, 6.51) * mm, v(-12.27, 6.43) * mm, v(-13.62, 7.12) * mm, v(-17.56, 9.04) * mm, v(-17.65, 9.08) * mm, v(-18.6, 17.58) * mm, v(-18.59, 17.63) * mm, v(-18.25, 17.64) * mm, v(-17, 17.78) * mm, v(-15.86, 18.08) * mm, v(-15.5, 18.29) * mm], "startDerivative": vector(-9.7, -0.12) * mm, "endDerivative": vector(21.44, 14.57) * mm});
            skSolve(sketch);
        }
        {
            var Q0;
            Q0 = qSketchRegion(id + "F32", true);
            extrude(context, id + "F33", {"entities" : qUnion([Q0]), "depth" : 1.83 * mm, "offsetDistance" : 25.4 * mm});
        }
        {
            var Q0;
            Q0=qCreatedBy(makeId("Front.planeOp"),FACE);
            var sketch = newSketch(context, id + "F34", { "sketchPlane" : qUnion([Q0])});
            skFitSpline(sketch, "E126", {"points": [v(-9.23, 19.22) * mm, v(-13.12, 22.47) * mm, v(-13.3, 22.43) * mm], "startDerivative": vector(-6.1, 5.61) * mm, "endDerivative": vector(-0.82, -0.6) * mm});
            skFitSpline(sketch, "E127", {"points": [v(-13.3, 22.43) * mm, v(-13.83, 21.32) * mm, v(-13.78, 20.83) * mm, v(-12.92, 18.42) * mm, v(-12.55, 17.03) * mm, v(-12.37, 15.96) * mm, v(-12.23, 14.68) * mm, v(-12.2, 14.07) * mm, v(-12.1, 13.96) * mm, v(-11.86, 14.19) * mm, v(-11.69, 14.5) * mm, v(-11.45, 14.86) * mm, v(-10.82, 15.33) * mm, v(-8.18, 15.99) * mm, v(-6.89, 16.27) * mm, v(-6.16, 16.32) * mm, v(-5.91, 16.34) * mm, v(-5.83, 16.62) * mm, v(-6.08, 16.89) * mm, v(-7.12, 17.65) * mm, v(-7.38, 17.78) * mm, v(-7.62, 17.68) * mm, v(-7.92, 17.3) * mm, v(-8.56, 16.94) * mm, v(-9.7, 16.8) * mm, v(-10.66, 16.92) * mm, v(-11.39, 17.65) * mm, v(-11.75, 18.42) * mm, v(-11.87, 19.4) * mm, v(-11.67, 19.8) * mm, v(-11.4, 19.97) * mm, v(-11.02, 19.94) * mm, v(-10.2, 19.45) * mm, v(-9.56, 19) * mm, v(-9.33, 18.88) * mm, v(-9.18, 19) * mm, v(-9.16, 19.11) * mm], "startDerivative": vector(-18.9, -33.88) * mm, "endDerivative": vector(0.16, 9.75) * mm});
            skFitSpline(sketch, "E128", {"points": [v(-9.16, 19.11) * mm, v(-9.23, 19.22) * mm], "startDerivative": vector(-0.07, 0.1) * mm, "endDerivative": vector(-0.07, 0.1) * mm});
            skSolve(sketch);
        }
        {
            var Q0;
            Q0 = qSketchRegion(id + "F34", true);
            extrude(context, id + "F35", {"entities" : qUnion([Q0]), "depth" : 1.83 * mm, "offsetDistance" : 25.4 * mm});
        }
        {
            var Q0;
            Q0=qCreatedBy(makeId("Front.planeOp"),FACE);
            var sketch = newSketch(context, id + "F36", { "sketchPlane" : qUnion([Q0])});
            skFitSpline(sketch, "E129", {"points": [v(-4.26, 14.6) * mm, v(-4.55, 14.46) * mm, v(-4.79, 13.95) * mm, v(-4.74, 13.29) * mm, v(-4.18, 12.64) * mm, v(-3.23, 12.42) * mm, v(-2.48, 12.6) * mm, v(-2.33, 12.98) * mm, v(-2.43, 13.5) * mm, v(-2.46, 13.73) * mm, v(-2.38, 13.85) * mm], "startDerivative": vector(-3.86, -1.05) * mm, "endDerivative": vector(2.04, 2.05) * mm});
            skFitSpline(sketch, "E130", {"points": [v(-2.38, 13.85) * mm, v(-1.25, 12.91) * mm, v(-0.8, 12.5) * mm, v(-0.6, 12.14) * mm, v(-0.85, 11.66) * mm, v(-1.25, 11.01) * mm, v(-1.71, 9.81) * mm, v(-1.84, 8.65) * mm, v(-1.71, 7.96) * mm, v(-1.7, 7.43) * mm, v(-1.95, 7.29) * mm], "startDerivative": vector(8.95, -7.3) * mm, "endDerivative": vector(-4.9, -1.47) * mm});
            skFitSpline(sketch, "E131", {"points": [v(-1.95, 7.29) * mm, v(-2.2, 7.29) * mm, v(-3.15, 7.17) * mm, v(-4.53, 6.72) * mm, v(-5.6, 6.23) * mm, v(-5.92, 6.13) * mm, v(-6.3, 6.53) * mm, v(-11.73, 12.61) * mm, v(-11.8, 12.91) * mm, v(-10.94, 14.24) * mm, v(-10.73, 14.3) * mm, v(-6.96, 15.37) * mm, v(-6.8, 15.28) * mm, v(-6.84, 14.98) * mm, v(-7.02, 14.88) * mm, v(-7.53, 14.6) * mm, v(-8.25, 13.44) * mm, v(-8.5, 12.5) * mm, v(-8.42, 11.44) * mm, v(-7.67, 9.87) * mm, v(-6.4, 8.7) * mm, v(-4.67, 8.61) * mm, v(-3.61, 9.05) * mm, v(-3, 9.94) * mm, v(-2.88, 10.92) * mm, v(-3.38, 11.63) * mm, v(-4.14, 11.93) * mm, v(-4.96, 11.89) * mm, v(-5.75, 11.5) * mm, v(-6.08, 10.86) * mm, v(-6.11, 10.35) * mm, v(-6.4, 10.18) * mm, v(-6.6, 10.24) * mm, v(-6.7, 11.13) * mm, v(-6.7, 12.2) * mm, v(-6.42, 13.14) * mm, v(-5.9, 13.85) * mm, v(-5.07, 14.52) * mm, v(-4.51, 14.82) * mm, v(-4.32, 14.8) * mm, v(-4.22, 14.73) * mm, v(-4.21, 14.65) * mm, v(-4.22, 14.62) * mm, v(-4.26, 14.6) * mm], "startDerivative": vector(-16.41, 0.45) * mm, "endDerivative": vector(-8.6, -3.95) * mm});
            skSolve(sketch);
        }
        {
            var Q0;
            Q0 = qSketchRegion(id + "F36", true);
            extrude(context, id + "F37", {"entities" : qUnion([Q0]), "depth" : 1.83 * mm, "offsetDistance" : 25.4 * mm});
        }
        {
            var Q0;
            Q0=qCreatedBy(makeId("Front.planeOp"),FACE);
            var sketch = newSketch(context, id + "F38", { "sketchPlane" : qUnion([Q0])});
            skFitSpline(sketch, "E132", {"points": [v(14.85, 13.09) * mm, v(15.19, 13.94) * mm, v(15.26, 14.6) * mm, v(14.98, 15.02) * mm, v(14.22, 14.93) * mm, v(12.43, 14.16) * mm, v(12.2, 13.77) * mm, v(12, 13.28) * mm, v(12.03, 13.18) * mm, v(12.43, 12.99) * mm, v(12.72, 12.34) * mm, v(12.83, 11.06) * mm, v(12.7, 10.06) * mm, v(12.76, 9.85) * mm, v(13.53, 9.52) * mm, v(15.37, 8.77) * mm, v(15.4, 8.97) * mm, v(15.38, 9.81) * mm, v(15.54, 10.81) * mm, v(16.35, 13.28) * mm, v(16.89, 14.46) * mm, v(16.9, 14.65) * mm, v(16.74, 14.64) * mm, v(16.46, 14.08) * mm, v(15.78, 12.63) * mm, v(15.16, 11.62) * mm, v(14.19, 10.9) * mm, v(13.54, 11.35) * mm, v(13.3, 11.94) * mm, v(13.17, 12.6) * mm, v(13.46, 13.55) * mm, v(13.92, 13.65) * mm, v(14.43, 13.28) * mm, v(14.56, 12.7) * mm, v(14.56, 12.44) * mm, v(14.7, 12.78) * mm, v(14.85, 13.09) * mm]});
            skSolve(sketch);
        }
        {
            var Q0;
            Q0=makeQuery(id+"F38.imprint","IMPRINT",FACE,{"disambiguationData":[TD([[makeQuery(id+"F38.imprint","IMPRINT",EDGE,{"derivedFrom":sQuery(id+"F38.wireOp",EDGE,"E132")}),1.0]])]});
            extrude(context, id + "F39", {"entities" : qUnion([Q0]), "depth" : 1.83 * mm, "offsetDistance" : 25.4 * mm});
        }
        {
            var Q0;
            Q0=qCreatedBy(makeId("Front.planeOp"),FACE);
            var sketch = newSketch(context, id + "F40", { "sketchPlane" : qUnion([Q0])});
            skFitSpline(sketch, "E133", {"points": [v(17.18, 12.87) * mm, v(17.18, 12.52) * mm, v(17.41, 11.7) * mm, v(17.88, 11.16) * mm, v(18.2, 11.49) * mm, v(18.3, 13.46) * mm, v(18.1, 17.55) * mm, v(18.1, 18.1) * mm, v(18.2, 17.82) * mm, v(18.56, 14.33) * mm, v(19.2, 12) * mm, v(19.92, 10.95) * mm, v(20.7, 10.83) * mm, v(21.54, 11.9) * mm, v(22.06, 13.24) * mm, v(22, 14.9) * mm, v(21.69, 15.89) * mm, v(21.34, 16.1) * mm, v(21.03, 16.03) * mm, v(20.62, 15.15) * mm, v(20.4, 13.83) * mm, v(20.23, 13.67) * mm, v(20.1, 14.86) * mm, v(20.04, 17.43) * mm, v(20.17, 17.57) * mm, v(22.74, 17.14) * mm, v(22.76, 16.92) * mm, v(23.37, 11.82) * mm, v(23.4, 11.76) * mm, v(22.1, 10.81) * mm, v(19.55, 8.55) * mm, v(19.49, 8.39) * mm, v(18.8, 9.25) * mm, v(16.8, 11.57) * mm, v(16.73, 11.82) * mm, v(16.88, 12.76) * mm, v(17, 12.9) * mm, v(17.1, 12.92) * mm, v(17.17, 12.92) * mm, v(17.18, 12.87) * mm]});
            skSolve(sketch);
        }
        {
            var Q0;
            Q0 = qSketchRegion(id + "F40", true);
            extrude(context, id + "F41", {"entities" : qUnion([Q0]), "depth" : 1.83 * mm, "offsetDistance" : 25.4 * mm});
        }
        {
            var Q0;
            Q0=qCreatedBy(makeId("Front.planeOp"),FACE);
            var sketch = newSketch(context, id + "F42", { "sketchPlane" : qUnion([Q0])});
            skFitSpline(sketch, "E134", {"points": [v(13.14, 16.77) * mm, v(13.23, 16.48) * mm, v(13.67, 16.35) * mm, v(14.28, 16.35) * mm, v(15.97, 17.16) * mm, v(16.66, 18.6) * mm, v(16.63, 19.65) * mm, v(15.95, 20.05) * mm, v(14.9, 19.53) * mm, v(14.16, 18.7) * mm, v(14.02, 18.68) * mm, v(14.11, 18.92) * mm, v(15.12, 20.31) * mm, v(16.26, 21.44) * mm, v(17.24, 21.98) * mm, v(17.39, 22.03) * mm, v(17.83, 20.85) * mm, v(17.88, 20.63) * mm, v(17.54, 19.39) * mm, v(17.37, 17.2) * mm, v(17.54, 15.67) * mm, v(17.56, 15.38) * mm, v(17.37, 15.28) * mm, v(16.97, 15.72) * mm, v(16.41, 16.04) * mm, v(15.6, 16.09) * mm, v(14.28, 15.72) * mm, v(12.84, 15.08) * mm, v(12.5, 14.91) * mm, v(12.35, 15.08) * mm, v(12.55, 15.72) * mm, v(12.92, 16.55) * mm, v(13.14, 16.77) * mm]});
            skSolve(sketch);
        }
        {
            var Q0;
            Q0 = qSketchRegion(id + "F42", true);
            extrude(context, id + "F43", {"entities" : qUnion([Q0]), "depth" : 1.83 * mm, "offsetDistance" : 25.4 * mm});
        }
        {
            var Q0;
            Q0=qCreatedBy(makeId("Front.planeOp"),FACE);
            var sketch = newSketch(context, id + "F44", { "sketchPlane" : qUnion([Q0])});
            skFitSpline(sketch, "E135", {"points": [v(24.17, 29.85) * mm, v(24.5, 28.86) * mm, v(25.5, 25.12) * mm, v(25.5, 24.9) * mm, v(25.12, 22.94) * mm, v(24.6, 19.57) * mm, v(24.57, 19.12) * mm, v(24.13, 18.98) * mm, v(22.67, 18.3) * mm, v(22.39, 18.07) * mm, v(21.23, 18.34) * mm, v(19.94, 18.44) * mm, v(19.84, 18.6) * mm, v(18.03, 22.4) * mm, v(18.03, 22.51) * mm, v(18.44, 22.72) * mm, v(20.9, 24.2) * mm, v(22.39, 25.57) * mm, v(23.25, 26.95) * mm, v(23.35, 27.34) * mm, v(23.5, 27.36) * mm, v(23.41, 25.76) * mm, v(22.84, 23.3) * mm, v(21.69, 21.55) * mm, v(21.36, 21.46) * mm, v(21.4, 21.71) * mm, v(21.75, 22.35) * mm, v(21.6, 23.03) * mm, v(21.1, 23.25) * mm, v(20.45, 23.23) * mm, v(19.94, 22.72) * mm, v(19.6, 21.38) * mm, v(19.88, 20.1) * mm, v(21.38, 19.22) * mm, v(22.65, 19.65) * mm, v(23.89, 22.3) * mm, v(24.3, 24.75) * mm, v(24.26, 27.49) * mm, v(24.17, 29.13) * mm, v(24.12, 29.73) * mm, v(24.13, 29.84) * mm, v(24.14, 29.86) * mm, v(24.16, 29.87) * mm, v(24.17, 29.85) * mm]});
            skSolve(sketch);
        }
        {
            var Q0;
            Q0 = qSketchRegion(id + "F44", true);
            extrude(context, id + "F45", {"entities" : qUnion([Q0]), "depth" : 1.83 * mm, "offsetDistance" : 25.4 * mm});
        }
        {
            var Q0;
            Q0=qCreatedBy(makeId("Front.planeOp"),FACE);
            var sketch = newSketch(context, id + "F46", { "sketchPlane" : qUnion([Q0])});
            skFitSpline(sketch, "E136", {"points": [v(26.1, 16.66) * mm, v(25.85, 17.2) * mm, v(25.06, 18.25) * mm, v(24.92, 18.37) * mm, v(24.06, 18.07) * mm, v(23.59, 17.83) * mm, v(23.53, 17.6) * mm, v(23.97, 14.14) * mm, v(24.19, 12.17) * mm, v(24.19, 12.14) * mm, v(26.27, 10.7) * mm, v(26.32, 10.73) * mm, v(27.3, 11.87) * mm, v(27.8, 12.43) * mm, v(28.04, 12.74) * mm, v(28.05, 12.81) * mm, v(27.96, 12.97) * mm, v(27.7, 12.81) * mm, v(27.17, 12.58) * mm, v(26.35, 12.71) * mm, v(25.67, 13.38) * mm, v(24.75, 15.24) * mm, v(24.7, 16.72) * mm, v(25.02, 17.09) * mm, v(25.6, 16.98) * mm, v(26.01, 16.48) * mm, v(26.12, 16.5) * mm, v(26.1, 16.66) * mm]});
            skSolve(sketch);
        }
        {
            var Q0;
            Q0 = qSketchRegion(id + "F46", true);
            extrude(context, id + "F47", {"entities" : qUnion([Q0]), "depth" : 1.83 * mm, "offsetDistance" : 25.4 * mm});
        }
        {
            var Q0;
            Q0=qCreatedBy(makeId("Front.planeOp"),FACE);
            var sketch = newSketch(context, id + "F48", { "sketchPlane" : qUnion([Q0])});
            skFitSpline(sketch, "E137", {"points": [v(26.43, 23.7) * mm, v(26.74, 21.87) * mm, v(27.7, 18.31) * mm, v(29.04, 15.46) * mm, v(30.03, 14.39) * mm, v(30.74, 14.5) * mm, v(30.9, 15.13) * mm, v(30.74, 16.6) * mm, v(30.1, 18.56) * mm, v(29.1, 20.97) * mm, v(28.41, 22.55) * mm, v(28.45, 22.75) * mm, v(28.6, 22.66) * mm, v(29.26, 21.47) * mm, v(30.4, 19.82) * mm, v(31.1, 19.08) * mm, v(31.75, 19.11) * mm, v(31.92, 19.7) * mm, v(31.32, 20.87) * mm, v(30.06, 22.76) * mm, v(29.75, 23.2) * mm, v(29.75, 23.4) * mm, v(30.78, 22.08) * mm, v(32.6, 19.77) * mm, v(32.77, 19.4) * mm, v(32.65, 19.02) * mm, v(31.73, 17.95) * mm, v(31.32, 17.24) * mm, v(31.46, 16.41) * mm, v(31.98, 14.7) * mm, v(32.84, 11.5) * mm, v(32.82, 11.42) * mm, v(31.42, 12.18) * mm, v(28.72, 13.46) * mm, v(28.59, 13.54) * mm, v(27.24, 16.22) * mm, v(25.94, 18.37) * mm, v(25.84, 18.49) * mm, v(25.98, 22.9) * mm, v(26.24, 23.73) * mm, v(26.33, 23.75) * mm, v(26.43, 23.7) * mm]});
            skSolve(sketch);
        }
        {
            var Q0;
            Q0 = qSketchRegion(id + "F48", true);
            extrude(context, id + "F49", {"entities" : qUnion([Q0]), "depth" : 1.83 * mm, "offsetDistance" : 25.4 * mm});
        }
        {
            var Q0;
            Q0=qCreatedBy(makeId("Front.planeOp"),FACE);
            var sketch = newSketch(context, id + "F50", { "sketchPlane" : qUnion([Q0])});
            skFitSpline(sketch, "E138", {"points": [v(30.87, 23.4) * mm, v(35.1, 23.44) * mm, v(35.17, 23.38) * mm, v(36.57, 21.47) * mm, v(36.85, 21.07) * mm, v(36.84, 21.03) * mm, v(36.7, 21.01) * mm, v(36.15, 21.57) * mm, v(35.55, 21.96) * mm, v(34.8, 21.98) * mm, v(34.5, 21.64) * mm, v(34.5, 21.17) * mm, v(34.85, 20.48) * mm, v(35.81, 19.75) * mm, v(36.86, 19.12) * mm, v(38.36, 19.07) * mm, v(39.42, 19.82) * mm, v(39.83, 21.25) * mm, v(39.7, 22.18) * mm, v(39.03, 23.43) * mm, v(37.46, 24.88) * mm, v(36.3, 25.4) * mm, v(35.6, 25.36) * mm, v(35.28, 25.16) * mm, v(35.2, 25.13) * mm, v(35.1, 25.54) * mm, v(34.82, 28.31) * mm, v(34.76, 28.6) * mm, v(34.81, 28.66) * mm, v(35.61, 27.9) * mm, v(37.45, 25.97) * mm, v(39.44, 24.09) * mm, v(40.25, 23.08) * mm, v(40.66, 22.17) * mm, v(40.98, 20.93) * mm, v(40.96, 19.9) * mm, v(40.68, 19.04) * mm, v(40.2, 17.63) * mm, v(40.13, 17.39) * mm, v(40.04, 17.32) * mm, v(37.81, 17.89) * mm, v(35.8, 18.34) * mm, v(34.74, 18.46) * mm, v(34.38, 18.84) * mm, v(31, 22.98) * mm, v(30.76, 23.27) * mm, v(30.77, 23.34) * mm, v(30.79, 23.39) * mm, v(30.87, 23.4) * mm]});
            skSolve(sketch);
        }
        {
            var Q0;
            Q0 = qSketchRegion(id + "F50", true);
            extrude(context, id + "F51", {"entities" : qUnion([Q0]), "depth" : 1.83 * mm, "offsetDistance" : 25.4 * mm});
        }
        {
            var Q0;
            Q0=qCreatedBy(makeId("Front.planeOp"),FACE);
            var sketch = newSketch(context, id + "F52", { "sketchPlane" : qUnion([Q0])});
            skFitSpline(sketch, "E139", {"points": [v(24.64, 32.15) * mm, v(24.79, 31.89) * mm, v(25.34, 30.24) * mm, v(27.2, 27.1) * mm, v(29.43, 25.26) * mm, v(31.76, 24.99) * mm, v(32.97, 25.72) * mm, v(33.34, 26.36) * mm, v(33.28, 27.9) * mm, v(32.46, 30.1) * mm, v(32.2, 30.41) * mm, v(31.92, 30.41) * mm, v(31.78, 30.01) * mm, v(31.97, 28.52) * mm, v(31.95, 27.21) * mm, v(31.54, 26.76) * mm, v(30.86, 26.78) * mm, v(29.56, 27.94) * mm, v(27.53, 30.47) * mm, v(26.93, 32.07) * mm, v(26.56, 33.18) * mm], "startDerivative": vector(6.14, -8.67) * mm, "endDerivative": vector(-8.15, 22.94) * mm});
            skFitSpline(sketch, "E140", {"points": [v(26.56, 33.18) * mm, v(26.35, 34.15) * mm, v(26.4, 34.2) * mm, v(26.78, 33.18) * mm, v(28.16, 30.57) * mm, v(29.71, 29.03) * mm, v(30.55, 28.7) * mm, v(31.02, 29.25) * mm, v(31.12, 30.58) * mm, v(30.59, 32.15) * mm, v(29.47, 33.97) * mm, v(28.45, 35.03) * mm, v(28.3, 35.16) * mm, v(28.39, 35.27) * mm, v(29, 35.03) * mm, v(30.68, 33.57) * mm, v(32.4, 31.63) * mm, v(33.48, 30.32) * mm, v(33.82, 29.9) * mm, v(33.84, 29.8) * mm, v(34.03, 27.51) * mm, v(34.27, 25.88) * mm, v(34.56, 24.27) * mm, v(34.54, 24.24) * mm, v(31.16, 24.19) * mm, v(26.88, 24.3) * mm, v(26.86, 24.32) * mm, v(26.05, 26.47) * mm, v(25.4, 28.3) * mm, v(24.79, 30.59) * mm, v(24.69, 31.55) * mm, v(24.66, 31.82) * mm, v(24.62, 32.08) * mm, v(24.62, 32.14) * mm, v(24.62, 32.15) * mm, v(24.62, 32.16) * mm, v(24.62, 32.16) * mm, v(24.63, 32.16) * mm, v(24.64, 32.16) * mm, v(24.64, 32.15) * mm], "startDerivative": vector(-13.44, 43.76) * mm, "endDerivative": vector(0.12, -2.54) * mm});
            skSolve(sketch);
        }
        {
            var Q0;
            Q0 = qSketchRegion(id + "F52", true);
            extrude(context, id + "F53", {"entities" : qUnion([Q0]), "depth" : 1.83 * mm, "offsetDistance" : 25.4 * mm});
        }
        {
            var Q0;
            Q0=qCreatedBy(makeId("Front.planeOp"),FACE);
            var sketch = newSketch(context, id + "F54", { "sketchPlane" : qUnion([Q0])});
            skFitSpline(sketch, "E141", {"points": [v(30.4, 36.29) * mm, v(30.97, 34.79) * mm, v(31.09, 34.56) * mm, v(33.2, 32.02) * mm, v(35.1, 29.75) * mm, v(35.25, 29.56) * mm, v(35.5, 29.79) * mm, v(35.74, 30.72) * mm, v(36.17, 32.56) * mm, v(36.57, 33.67) * mm, v(36.62, 34.12) * mm, v(36.6, 34.3) * mm, v(36.34, 34.25) * mm, v(36.04, 33.67) * mm, v(35.5, 33.24) * mm, v(34.06, 33.17) * mm, v(32.76, 34.13) * mm, v(32.73, 34.94) * mm, v(33.19, 35.16) * mm, v(34.03, 34.96) * mm, v(34.72, 34.6) * mm, v(34.83, 34.64) * mm, v(34.87, 34.82) * mm, v(34.44, 35.25) * mm, v(31.9, 36.09) * mm, v(30.5, 36.44) * mm, v(30.36, 36.41) * mm, v(30.4, 36.29) * mm]});
            skSolve(sketch);
        }
        {
            var Q0;
            Q0 = qSketchRegion(id + "F54", true);
            extrude(context, id + "F55", {"entities" : qUnion([Q0]), "depth" : 1.83 * mm, "offsetDistance" : 25.4 * mm});
        }
        {
            var Q0;
            Q0=qCreatedBy(makeId("Front.planeOp"),FACE);
            var sketch = newSketch(context, id + "F56", { "sketchPlane" : qUnion([Q0])});
            skFitSpline(sketch, "E142", {"points": [v(37.57, 34.39) * mm, v(38.58, 33.98) * mm, v(38.6, 33.7) * mm, v(39.59, 31.48) * mm, v(41.23, 29.45) * mm, v(42.28, 28.98) * mm, v(42.78, 29.31) * mm, v(42.84, 30.36) * mm, v(42.34, 31.54) * mm, v(41.56, 32.74) * mm, v(41.04, 33.2) * mm, v(40.9, 33.5) * mm, v(40.98, 33.75) * mm, v(41.23, 33.77) * mm, v(42.18, 33.26) * mm, v(46.7, 30.4) * mm, v(46.81, 30.36) * mm, v(48.3, 26.66) * mm, v(48.3, 26.54) * mm, v(46.58, 24.18) * mm, v(46.45, 23.96) * mm, v(41.04, 23.58) * mm], "startDerivative": vector(29.95, -8.78) * mm, "endDerivative": vector(-74.37, -3.28) * mm});
            skFitSpline(sketch, "E143", {"points": [v(41.04, 23.58) * mm, v(36.14, 28.8) * mm, v(36.04, 28.94) * mm, v(36.62, 31.87) * mm, v(36.76, 31.99) * mm, v(36.9, 31.77) * mm, v(37.45, 29.85) * mm, v(39.7, 26.66) * mm, v(41.95, 24.91) * mm, v(44.72, 24.72) * mm, v(46.15, 26.37) * mm, v(46.15, 28.5) * mm, v(45.1, 30.47) * mm, v(43.56, 31.62) * mm, v(43.27, 31.56) * mm, v(43.19, 31.15) * mm, v(44.4, 29.49) * mm, v(44.66, 27.57) * mm, v(44.06, 26.77) * mm, v(42.67, 26.97) * mm, v(41.04, 28) * mm, v(39.4, 29.62) * mm, v(38.23, 31.27) * mm, v(37.65, 32.37) * mm, v(37.34, 32.82) * mm, v(37.3, 32.93) * mm, v(37.36, 33.92) * mm, v(37.38, 34.33) * mm, v(37.45, 34.39) * mm, v(37.57, 34.39) * mm], "startDerivative": vector(-83.26, 91.88) * mm, "endDerivative": vector(11.9, -1.2) * mm});
            skSolve(sketch);
        }
        {
            var Q0;
            Q0 = qSketchRegion(id + "F56", true);
            extrude(context, id + "F57", {"entities" : qUnion([Q0]), "depth" : 1.83 * mm, "offsetDistance" : 25.4 * mm});
        }
        {
            var Q0;
            Q0=qCreatedBy(makeId("Front.planeOp"),FACE);
            var sketch = newSketch(context, id + "F58", { "sketchPlane" : qUnion([Q0])});
            skFitSpline(sketch, "E144", {"points": [v(49.26, 35.88) * mm, v(48.38, 35.7) * mm, v(48.28, 35.08) * mm, v(49.29, 34.04) * mm, v(50.51, 33.52) * mm, v(50.77, 33.39) * mm, v(50.6, 33.25) * mm, v(49.04, 33.61) * mm, v(47.68, 34.38) * mm, v(46.68, 35.65) * mm, v(46.36, 36.6) * mm, v(46.32, 37.07) * mm, v(46.4, 37.21) * mm, v(47.77, 37.38) * mm, v(51.59, 37.6) * mm, v(52.1, 37.44) * mm, v(55.35, 34.2) * mm, v(56.76, 32.7) * mm, v(56.8, 32.6) * mm, v(54.94, 31.43) * mm, v(52.56, 30.12) * mm, v(52.28, 30.1) * mm, v(47.52, 30.73) * mm, v(47.38, 30.73) * mm, v(44.13, 32.86) * mm, v(42.32, 33.9) * mm, v(42.1, 34.03) * mm, v(42.1, 34.12) * mm, v(43.4, 34.59) * mm, v(44.67, 34.96) * mm, v(44.73, 35) * mm, v(44.8, 34.65) * mm, v(46.35, 33.04) * mm, v(48.99, 31.7) * mm, v(51, 31.53) * mm, v(52.73, 32.05) * mm, v(53.21, 33.02) * mm, v(53.08, 34.38) * mm, v(51.95, 35.29) * mm, v(50.25, 35.73) * mm, v(49.26, 35.88) * mm]});
            skSolve(sketch);
        }
        {
            var Q0;
            Q0 = qSketchRegion(id + "F58", true);
            extrude(context, id + "F59", {"entities" : qUnion([Q0]), "depth" : 1.83 * mm, "offsetDistance" : 25.4 * mm});
        }
        {
            var Q0;
            Q0=qCreatedBy(makeId("Front.planeOp"),FACE);
            var sketch = newSketch(context, id + "F60", { "sketchPlane" : qUnion([Q0])});
            skFitSpline(sketch, "E145", {"points": [v(30.66, 37.05) * mm, v(31.91, 37.33) * mm, v(34.55, 36.93) * mm, v(38.51, 35.94) * mm, v(41.38, 35.73) * mm, v(43.53, 36.23) * mm, v(43.75, 36.78) * mm, v(43.54, 37.2) * mm, v(42.98, 37.4) * mm, v(43.02, 37.47) * mm, v(43.95, 37.43) * mm, v(45.3, 37) * mm, v(45.46, 36.9) * mm, v(45.53, 36.26) * mm, v(45.38, 36.13) * mm, v(40.11, 34.37) * mm, v(39.55, 34.07) * mm, v(39.28, 34.06) * mm, v(39.13, 34.36) * mm, v(37.39, 35.13) * mm, v(34.83, 35.95) * mm, v(32.03, 36.64) * mm, v(30.72, 36.87) * mm, v(30.58, 36.95) * mm, v(30.58, 37) * mm, v(30.6, 37.03) * mm, v(30.66, 37.05) * mm]});
            skSolve(sketch);
        }
        {
            var Q0;
            Q0 = qSketchRegion(id + "F60", true);
            extrude(context, id + "F61", {"entities" : qUnion([Q0]), "depth" : 1.83 * mm, "offsetDistance" : 25.4 * mm});
        }
        {
            var Q0;
            Q0=qCreatedBy(makeId("Front.planeOp"),FACE);
            var sketch = newSketch(context, id + "F62", { "sketchPlane" : qUnion([Q0])});
            skFitSpline(sketch, "E146", {"points": [v(31.51, 42.4) * mm, v(31.49, 41.88) * mm, v(30.71, 40.12) * mm, v(29.22, 38.16) * mm, v(28.56, 37.75) * mm, v(28.4, 37.64) * mm, v(28.83, 37.4) * mm, v(29.43, 37.13) * mm, v(29.82, 37.6) * mm, v(33.2, 38.78) * mm, v(37.65, 38.82) * mm, v(43.07, 37.9) * mm, v(44.5, 37.54) * mm, v(44.57, 37.54) * mm, v(45.47, 38.95) * mm, v(46.9, 40.9) * mm, v(47.91, 42.05) * mm, v(47.9, 42.17) * mm, v(46.95, 42.48) * mm, v(45.7, 42.76) * mm, v(45.5, 42.82) * mm, v(44.93, 41.94) * mm, v(44.78, 41.64) * mm, v(45.1, 41.48) * mm, v(45.4, 40.83) * mm, v(44.72, 39.82) * mm, v(43.13, 39.13) * mm, v(40.47, 39.1) * mm, v(38.94, 39.35) * mm, v(38.5, 39.57) * mm, v(38.47, 40.02) * mm, v(38.95, 40.34) * mm, v(40.14, 40.58) * mm, v(41.76, 40.61) * mm, v(42.35, 40.61) * mm, v(42.4, 40.79) * mm, v(41.79, 40.91) * mm, v(38.28, 40.89) * mm, v(35.87, 40.54) * mm, v(33.05, 39.64) * mm, v(31.66, 39.08) * mm, v(31.3, 39) * mm, v(31.14, 39.12) * mm, v(31.36, 39.7) * mm, v(32.07, 40.19) * mm, v(34.87, 41.38) * mm, v(38.23, 42.02) * mm, v(41.95, 42.15) * mm, v(43.7, 41.86) * mm, v(44.1, 41.72) * mm, v(44.3, 41.82) * mm, v(46.17, 45.6) * mm, v(47.27, 47.57) * mm, v(47.43, 47.92) * mm, v(46.45, 47.87) * mm, v(44.82, 47.55) * mm, v(44.73, 47.44) * mm, v(44.27, 46.15) * mm, v(44.28, 46.04) * mm, v(44.63, 46.12) * mm, v(45.23, 46.07) * mm, v(45.42, 45.6) * mm, v(44.84, 44.4) * mm, v(43.34, 43.52) * mm, v(41.93, 43.26) * mm, v(41.58, 43.31) * mm, v(41.7, 43.91) * mm, v(42.4, 44.16) * mm, v(42.84, 44.23) * mm, v(42.91, 44.4) * mm, v(41.67, 44.3) * mm, v(37.79, 43.31) * mm, v(33.75, 41.7) * mm, v(32.3, 41.3) * mm, v(32, 41.52) * mm, v(32.2, 42.28) * mm, v(33.21, 43.42) * mm, v(38.03, 47.12) * mm, v(42.06, 49.16) * mm, v(42.68, 49.18) * mm, v(43.14, 48.84) * mm, v(43, 47.97) * mm, v(41.45, 46.55) * mm, v(39.87, 45.8) * mm, v(39.16, 45.66) * mm, v(38.99, 45.76) * mm, v(39.37, 46.48) * mm, v(40.36, 47.07) * mm, v(40.58, 47.23) * mm, v(40.54, 47.4) * mm, v(40.08, 47.27) * mm, v(35.57, 44.52) * mm, v(34.04, 43.13) * mm, v(33.07, 42.28) * mm, v(33.04, 42.17) * mm, v(33.17, 42.15) * mm, v(34.13, 42.64) * mm, v(36.8, 43.7) * mm, v(40.68, 45.05) * mm, v(43.49, 45.77) * mm, v(43.58, 45.8) * mm, v(44.1, 47.5) * mm, v(45.72, 51.47) * mm, v(46.1, 52.1) * mm, v(46.26, 52.4) * mm, v(46.15, 52.57) * mm, v(44.7, 52.1) * mm, v(39.48, 49.22) * mm, v(31.82, 42.84) * mm, v(31.53, 42.53) * mm, v(31.51, 42.4) * mm]});
            skSolve(sketch);
        }
        {
            var Q0;
            Q0 = qSketchRegion(id + "F62", true);
            extrude(context, id + "F63", {"entities" : qUnion([Q0]), "depth" : 1.83 * mm, "offsetDistance" : 25.4 * mm});
        }
        {
            var Q0;
            Q0=qCreatedBy(makeId("Front.planeOp"),FACE);
            var sketch = newSketch(context, id + "F64", { "sketchPlane" : qUnion([Q0])});
            skFitSpline(sketch, "E147", {"points": [v(45.64, 38.1) * mm, v(45.55, 37.69) * mm, v(46.65, 37.95) * mm, v(52.05, 38.14) * mm, v(56.28, 37.95) * mm, v(59.74, 37.23) * mm, v(61.81, 36.63) * mm, v(62.26, 36.47) * mm, v(62.4, 36.5) * mm, v(61.76, 37.15) * mm, v(57.54, 39.82) * mm, v(52.56, 42.06) * mm, v(51.1, 42.42) * mm, v(50.22, 42.4) * mm, v(48.93, 41.8) * mm, v(48.38, 41.34) * mm, v(48.44, 41.27) * mm, v(50.15, 41.4) * mm, v(54.69, 40.35) * mm, v(56, 39.51) * mm, v(56.26, 39.1) * mm, v(55.99, 38.96) * mm, v(53.78, 39.57) * mm, v(50.73, 40.4) * mm, v(48.44, 40.72) * mm, v(47.71, 40.66) * mm, v(45.64, 38.1) * mm]});
            skPoint(sketch, "E148", {"position": v(51.8, 42.29) * mm});
            skSolve(sketch);
        }
        {
            var Q0;
            Q0 = qSketchRegion(id + "F64", true);
            extrude(context, id + "F65", {"entities" : qUnion([Q0]), "depth" : 1.83 * mm, "offsetDistance" : 25.4 * mm});
        }
        {
            var Q0;
            Q0=qCreatedBy(makeId("Front.planeOp"),FACE);
            var sketch = newSketch(context, id + "F66", { "sketchPlane" : qUnion([Q0])});
            skFitSpline(sketch, "E149", {"points": [v(49.56, 39.91) * mm, v(48.65, 39.8) * mm, v(48.35, 39.58) * mm, v(48.39, 39.32) * mm, v(49.88, 38.9) * mm, v(51.55, 38.75) * mm, v(53, 38.68) * mm, v(53.2, 38.82) * mm, v(53.2, 39.12) * mm, v(52.43, 39.45) * mm, v(50.39, 39.86) * mm, v(49.56, 39.91) * mm]});
            skSolve(sketch);
        }
        {
            var Q0;
            Q0 = qSketchRegion(id + "F66", true);
            extrude(context, id + "F67", {"entities" : qUnion([Q0]), "operationType" : NewBodyOperationType.REMOVE, "depth" : 23.88 * mm, "offsetDistance" : 25.4 * mm});
        }
        {
            var Q0;
            Q0=qCreatedBy(makeId("Front.planeOp"),FACE);
            var sketch = newSketch(context, id + "F68", { "sketchPlane" : qUnion([Q0])});
            skFitSpline(sketch, "E150", {"points": [v(46.72, 44.89) * mm, v(46.26, 43.99) * mm, v(46.15, 43.53) * mm, v(47.76, 43.02) * mm, v(48.82, 42.6) * mm, v(49.74, 43.02) * mm, v(55.64, 44.61) * mm, v(61.03, 44.91) * mm, v(65.76, 44.54) * mm, v(67.12, 44.06) * mm, v(67.25, 44.06) * mm, v(67.32, 44.27) * mm, v(65.73, 45.19) * mm, v(62.76, 46.6) * mm, v(60.2, 47.51) * mm, v(54.67, 48.62) * mm, v(54.1, 48.71) * mm, v(52.02, 47.7) * mm, v(51.98, 47.6) * mm, v(52.97, 47.77) * mm, v(55.96, 47.95) * mm, v(59.56, 47.26) * mm, v(60.11, 46.9) * mm, v(60.09, 46.73) * mm, v(58.17, 46.66) * mm, v(53.98, 46.66) * mm, v(50.64, 46.22) * mm, v(47.76, 45.35) * mm, v(46.72, 44.89) * mm]});
            skSolve(sketch);
        }
        {
            var Q0;
            Q0 = qSketchRegion(id + "F68", true);
            extrude(context, id + "F69", {"entities" : qUnion([Q0]), "depth" : 1.83 * mm, "offsetDistance" : 25.4 * mm});
        }
        {
            var Q0;
            Q0=qCreatedBy(makeId("Front.planeOp"),FACE);
            var sketch = newSketch(context, id + "F70", { "sketchPlane" : qUnion([Q0])});
            skFitSpline(sketch, "E151", {"points": [v(50.46, 45.3) * mm, v(49.89, 44.9) * mm, v(49.76, 44.58) * mm, v(50.13, 44.5) * mm, v(54.23, 44.89) * mm, v(57.2, 45.36) * mm, v(57.68, 45.64) * mm, v(57.7, 45.77) * mm, v(56.3, 46.04) * mm, v(52.74, 45.84) * mm, v(50.84, 45.43) * mm, v(50.46, 45.3) * mm]});
            skSolve(sketch);
        }
        {
            var Q0;
            Q0 = qSketchRegion(id + "F70", true);
            extrude(context, id + "F71", {"entities" : qUnion([Q0]), "operationType" : NewBodyOperationType.REMOVE, "depth" : 25.4 * mm, "offsetDistance" : 25.4 * mm});
        }
        {
            var Q0;
            Q0=qCreatedBy(makeId("Front.planeOp"),FACE);
            var sketch = newSketch(context, id + "F72", { "sketchPlane" : qUnion([Q0])});
            skFitSpline(sketch, "E152", {"points": [v(69.72, 53.15) * mm, v(70.15, 53.12) * mm, v(70.32, 53.13) * mm, v(70.26, 53.3) * mm, v(69.43, 53.56) * mm, v(67.55, 53.97) * mm, v(64.58, 54.51) * mm, v(60.53, 54.51) * mm, v(54.7, 53.7) * mm, v(48.7, 52.03) * mm, v(46.23, 51.18) * mm, v(45.96, 50.85) * mm, v(46.02, 50.67) * mm, v(47.28, 51) * mm, v(53.23, 52.79) * mm, v(57.7, 53.66) * mm, v(60.44, 53.9) * mm, v(61.48, 53.85) * mm, v(61.54, 53.58) * mm, v(60.48, 53.3) * mm, v(56.58, 52.69) * mm, v(49.28, 50.8) * mm, v(45.46, 49.47) * mm, v(45.34, 49.2) * mm, v(45.1, 48.4) * mm, v(45.1, 48.27) * mm, v(46.08, 48.45) * mm, v(48.17, 48.54) * mm, v(48.23, 48.33) * mm, v(47.45, 46.45) * mm, v(47.32, 45.96) * mm, v(47.73, 46.04) * mm, v(50.96, 47.84) * mm, v(54.62, 49.5) * mm, v(60.63, 51.49) * mm, v(64.24, 52.3) * mm, v(67.86, 52.94) * mm, v(69.72, 53.15) * mm]});
            skSolve(sketch);
        }
        {
            var Q0;
            Q0 = qSketchRegion(id + "F72", true);
            extrude(context, id + "F73", {"entities" : qUnion([Q0]), "depth" : 1.83 * mm, "offsetDistance" : 25.4 * mm});
        }
        {
            var Q0;
            Q0=qCreatedBy(makeId("Front.planeOp"),FACE);
            var sketch = newSketch(context, id + "F74", { "sketchPlane" : qUnion([Q0])});
            skFitSpline(sketch, "E153", {"points": [v(51.4, 50.48) * mm, v(50.36, 49.84) * mm, v(50.28, 49.4) * mm, v(51.43, 49.28) * mm, v(55.61, 50.65) * mm, v(58.77, 51.62) * mm, v(59.4, 52.01) * mm, v(58.96, 52.15) * mm, v(55.75, 51.74) * mm, v(51.91, 50.62) * mm, v(51.4, 50.48) * mm]});
            skSolve(sketch);
        }
        {
            var Q0;
            Q0 = qSketchRegion(id + "F74", true);
            extrude(context, id + "F75", {"entities" : qUnion([Q0]), "operationType" : NewBodyOperationType.REMOVE, "depth" : 25.4 * mm, "offsetDistance" : 25.4 * mm});
        }
        {
            var Q0;
            Q0=qCreatedBy(makeId("Front.planeOp"),FACE);
            var sketch = newSketch(context, id + "F76", { "sketchPlane" : qUnion([Q0])});
            skFitSpline(sketch, "E154", {"points": [v(-26.26, 47.43) * mm, v(-25.39, 45.22) * mm, v(-23.6, 43.2) * mm, v(-20.17, 42.28) * mm, v(-17.75, 42.6) * mm, v(-17.62, 43.05) * mm, v(-17.62, 44.45) * mm, v(-18.49, 46.21) * mm, v(-18.55, 46.4) * mm, v(-18.4, 46.54) * mm, v(-17.42, 45.22) * mm, v(-16.53, 43.03) * mm, v(-16.36, 41.23) * mm, v(-16.67, 40.69) * mm, v(-17.15, 40.92) * mm, v(-19.79, 41.56) * mm, v(-21.37, 41.48) * mm, v(-21.84, 41.3) * mm, v(-20.83, 40.79) * mm, v(-17.29, 40.24) * mm, v(-17.1, 40.15) * mm, v(-17.2, 40.03) * mm, v(-22.52, 39.97) * mm, v(-23.3, 40.07) * mm, v(-24.2, 40.84) * mm, v(-25.77, 43.4) * mm, v(-26.32, 45.32) * mm, v(-26.45, 46.74) * mm, v(-26.26, 47.43) * mm]});
            skSolve(sketch);
        }
        {
            var Q0;
            Q0=qCreatedBy(makeId("Front.planeOp"),FACE);
            var sketch = newSketch(context, id + "F77", { "sketchPlane" : qUnion([Q0])});
            skFitSpline(sketch, "E155", {"points": [v(-20.43, 48.65) * mm, v(-20.57, 48.7) * mm, v(-20.46, 48.86) * mm, v(-19.46, 48.7) * mm, v(-17.33, 47.58) * mm, v(-15.48, 45.6) * mm, v(-14.33, 44.16) * mm, v(-12.28, 43) * mm, v(-11.04, 42.97) * mm, v(-10.92, 42.94) * mm, v(-11.77, 42.42) * mm, v(-14.46, 39.75) * mm, v(-15.05, 38.54) * mm, v(-15.6, 36.98) * mm, v(-15.76, 34.3) * mm, v(-14.59, 31.3) * mm, v(-13.5, 29.82) * mm, v(-13.08, 29.48) * mm, v(-13.1, 29.27) * mm, v(-13.39, 28.65) * mm, v(-13.44, 28.52) * mm, v(-13.63, 28.75) * mm, v(-13.94, 29.2) * mm, v(-15.48, 31.38) * mm, v(-16.68, 33.44) * mm, v(-17.15, 35.23) * mm, v(-17.14, 36.94) * mm, v(-15.96, 39.87) * mm, v(-15.58, 40.93) * mm, v(-15.6, 42.78) * mm, v(-16.43, 44.9) * mm, v(-18.16, 47.28) * mm, v(-19.78, 48.43) * mm, v(-20.23, 48.6) * mm, v(-20.43, 48.65) * mm]});
            skSolve(sketch);
        }
        {
            var Q0;
            Q0 = qSketchRegion(id + "F77", true);
            extrude(context, id + "F78", {"entities" : qUnion([Q0]), "depth" : 1.83 * mm, "offsetDistance" : 25.4 * mm});
        }
        {
            var Q0;
            Q0=qCreatedBy(makeId("Front.planeOp"),FACE);
            var sketch = newSketch(context, id + "F79", { "sketchPlane" : qUnion([Q0])});
            skFitSpline(sketch, "E156", {"points": [v(-14.25, 38.88) * mm, v(-13.33, 40.22) * mm, v(-12.98, 40.58) * mm, v(-12.88, 40.61) * mm, v(-12.65, 39.37) * mm, v(-12.45, 37.68) * mm, v(-12.88, 35.27) * mm, v(-13, 35.17) * mm, v(-13.2, 35.33) * mm, v(-13.07, 36.18) * mm, v(-13.6, 37.94) * mm, v(-13.97, 38.52) * mm, v(-14.17, 38.71) * mm, v(-14.24, 38.8) * mm, v(-14.27, 38.85) * mm, v(-14.25, 38.88) * mm]});
            skSolve(sketch);
        }
        {
            var Q0;
            Q0 = qSketchRegion(id + "F79", true);
            extrude(context, id + "F80", {"entities" : qUnion([Q0]), "depth" : 1.83 * mm, "offsetDistance" : 25.4 * mm});
        }
        {
            var Q0;
            Q0 = qSketchRegion(id + "F76", true);
            extrude(context, id + "F81", {"entities" : qUnion([Q0]), "depth" : 1.83 * mm, "offsetDistance" : 25.4 * mm});
        }
        {
            var Q0;
            Q0=qCreatedBy(makeId("Front.planeOp"),FACE);
            var sketch = newSketch(context, id + "F82", { "sketchPlane" : qUnion([Q0])});
            skFitSpline(sketch, "E157", {"points": [v(-26.31, 36.82) * mm, v(-25.68, 38.05) * mm, v(-24.34, 39) * mm, v(-23.26, 39.24) * mm, v(-19.78, 39.08) * mm, v(-18.13, 39.16) * mm, v(-17.33, 39.34) * mm, v(-17.15, 39.08) * mm, v(-17.79, 37.44) * mm, v(-17.99, 33.98) * mm, v(-17.43, 31.02) * mm, v(-16.36, 28.74) * mm, v(-15.95, 28.48) * mm, v(-15.78, 28.9) * mm, v(-16.1, 30.36) * mm, v(-16.75, 31.8) * mm, v(-16.9, 32.25) * mm, v(-16.79, 32.41) * mm, v(-16.5, 31.83) * mm, v(-14.21, 27.95) * mm, v(-14.19, 27.73) * mm, v(-15.6, 26.9) * mm, v(-16.38, 26.92) * mm, v(-16.43, 27.06) * mm, v(-16.86, 28.25) * mm, v(-18.97, 33.12) * mm, v(-20.25, 35.65) * mm, v(-21.4, 36.97) * mm, v(-22.92, 37.6) * mm, v(-24.48, 37.6) * mm, v(-26.04, 36.79) * mm, v(-26.24, 36.63) * mm, v(-26.34, 36.7) * mm, v(-26.31, 36.82) * mm]});
            skSolve(sketch);
        }
        {
            var Q0;
            Q0 = qSketchRegion(id + "F82", true);
            extrude(context, id + "F83", {"entities" : qUnion([Q0]), "depth" : 1.83 * mm, "offsetDistance" : 25.4 * mm});
        }
        {
            var Q0;
            Q0=qCreatedBy(makeId("Front.planeOp"),FACE);
            var sketch = newSketch(context, id + "F84", { "sketchPlane" : qUnion([Q0])});
            skFitSpline(sketch, "E158", {"points": [v(-15.32, 26.46) * mm, v(-14.9, 26.57) * mm, v(-13.03, 27.9) * mm, v(-12.6, 29.25) * mm, v(-12.51, 29.58) * mm, v(-12.32, 28.72) * mm, v(-11.87, 27.09) * mm, v(-10.33, 24.81) * mm, v(-7.2, 21.95) * mm, v(-3.53, 19.17) * mm, v(-1.44, 18.72) * mm, v(0, 19.03) * mm, v(0.4, 19.15) * mm, v(0.43, 18.84) * mm, v(-0.8, 17.5) * mm, v(-1.73, 16.83) * mm, v(-1.8, 16.85) * mm, v(-5.97, 20.22) * mm, v(-8.67, 22.42) * mm, v(-11.2, 24.1) * mm, v(-14, 25.6) * mm, v(-15.43, 26.19) * mm, v(-15.65, 26.4) * mm, v(-15.32, 26.46) * mm]});
            skSolve(sketch);
        }
        {
            var Q0;
            Q0=makeQuery(id+"F84.imprint","IMPRINT",FACE,{"disambiguationData":[TD([[makeQuery(id+"F84.imprint","IMPRINT",EDGE,{"derivedFrom":sQuery(id+"F84.wireOp",EDGE,"E158")}),-1.0]])]});
            extrude(context, id + "F85", {"entities" : qUnion([Q0]), "depth" : 1.83 * mm, "offsetDistance" : 25.4 * mm});
        }
        {
            var Q0;
            Q0=qCreatedBy(makeId("Front.planeOp"),FACE);
            var sketch = newSketch(context, id + "F86", { "sketchPlane" : qUnion([Q0])});
            skFitSpline(sketch, "E159", {"points": [v(-14.26, 24.63) * mm, v(-14.48, 24.79) * mm, v(-14.4, 25) * mm, v(-14.03, 24.75) * mm, v(-12.05, 23.61) * mm, v(-8.27, 21.12) * mm, v(-5.9, 19.1) * mm, v(-3.46, 16.94) * mm, v(-1.65, 15.52) * mm, v(-0.51, 15.66) * mm, v(0.74, 17.11) * mm, v(1.78, 18.73) * mm, v(1.54, 19.6) * mm, v(0.72, 20) * mm, v(-1.21, 19.77) * mm, v(-2.98, 20) * mm, v(-6.1, 21.92) * mm, v(-9.52, 24.9) * mm, v(-10.26, 25.76) * mm, v(-10.34, 26.04) * mm, v(-10.2, 26.22) * mm, v(-9.88, 25.8) * mm, v(-8.05, 24) * mm, v(-4.72, 21.4) * mm, v(-1.7, 20.4) * mm, v(0.88, 20.92) * mm, v(0.9, 20.88) * mm, v(2.56, 19.92) * mm, v(2.6, 19.8) * mm, v(2.54, 19.33) * mm, v(2.75, 17.61) * mm, v(2.73, 17.47) * mm, v(1.64, 16.62) * mm, v(0.34, 14.76) * mm, v(-0.17, 13.35) * mm, v(-0.2, 13.33) * mm, v(-2, 15.02) * mm, v(-5.54, 17.67) * mm, v(-7.27, 19.2) * mm, v(-8.98, 20.58) * mm, v(-10.62, 21.86) * mm, v(-11.53, 22.63) * mm, v(-12.33, 23.2) * mm, v(-13.57, 24.03) * mm, v(-14.26, 24.63) * mm]});
            skSolve(sketch);
        }
        {
            var Q0;
            Q0 = qSketchRegion(id + "F86", true);
            extrude(context, id + "F87", {"entities" : qUnion([Q0]), "depth" : 1.83 * mm, "offsetDistance" : 25.4 * mm});
        }
        {
            var Q0;
            Q0=qCreatedBy(makeId("Front.planeOp"),FACE);
            var sketch = newSketch(context, id + "F88", { "sketchPlane" : qUnion([Q0])});
            skFitSpline(sketch, "E160", {"points": [v(30.85, 44.38) * mm, v(30.89, 42.07) * mm, v(29.56, 39.44) * mm, v(27.46, 37.86) * mm, v(24.18, 37.46) * mm, v(23.14, 37.56) * mm, v(22.97, 37.76) * mm, v(23.53, 37.82) * mm, v(25.98, 38) * mm, v(27.15, 38.55) * mm, v(27.3, 38.89) * mm, v(26.42, 39.21) * mm, v(24.7, 38.89) * mm, v(23.06, 38.09) * mm, v(22.9, 38.06) * mm, v(22.7, 38.15) * mm, v(22.53, 39.9) * mm, v(23.25, 42.03) * mm, v(24.13, 43.4) * mm, v(24.6, 43.7) * mm, v(24.37, 43.32) * mm, v(23.73, 41.9) * mm, v(23.57, 40.17) * mm, v(23.84, 39.67) * mm, v(25.68, 39.58) * mm, v(28.32, 40.82) * mm, v(30.41, 43.69) * mm, v(30.85, 44.38) * mm]});
            skSolve(sketch);
        }
        {
            var Q0;
            Q0 = qSketchRegion(id + "F88", true);
            extrude(context, id + "F89", {"entities" : qUnion([Q0]), "depth" : 1.83 * mm, "offsetDistance" : 25.4 * mm});
        }
        {
            var Q0;
            Q0=qCreatedBy(makeId("Front.planeOp"),FACE);
            var sketch = newSketch(context, id + "F90", { "sketchPlane" : qUnion([Q0])});
            skFitSpline(sketch, "E161", {"points": [v(22.22, 30.39) * mm, v(21.84, 29.81) * mm, v(21.32, 28.63) * mm, v(21.24, 28.22) * mm, v(21.36, 28) * mm, v(22.1, 28.63) * mm, v(22.71, 30.23) * mm, v(23.2, 33.5) * mm, v(22.95, 36.85) * mm, v(22.95, 36.97) * mm, v(23.35, 36.77) * mm, v(26.18, 37.1) * mm, v(28.47, 37.04) * mm, v(29.77, 36.05) * mm, v(29.99, 35.4) * mm, v(30, 35.3) * mm, v(29.47, 35.69) * mm, v(28.41, 36.19) * mm, v(27.42, 36.25) * mm, v(25.56, 35.53) * mm, v(24.43, 34.18) * mm, v(23.83, 32.36) * mm, v(23.3, 29.83) * mm, v(22.48, 27.92) * mm, v(21.74, 26.98) * mm, v(21.46, 26.74) * mm, v(20.9, 26.9) * mm, v(20.36, 27.26) * mm, v(20.34, 27.52) * mm, v(20.8, 28.63) * mm, v(21.68, 30.05) * mm, v(22.06, 30.55) * mm, v(22.13, 30.58) * mm, v(22.2, 30.54) * mm, v(22.23, 30.48) * mm, v(22.22, 30.39) * mm]});
            skSolve(sketch);
        }
        {
            var Q0;
            Q0 = qSketchRegion(id + "F90", true);
            extrude(context, id + "F91", {"entities" : qUnion([Q0]), "depth" : 1.83 * mm, "offsetDistance" : 25.4 * mm});
        }
        {
            var Q0;
            Q0=qCreatedBy(makeId("Front.planeOp"),FACE);
            var sketch = newSketch(context, id + "F92", { "sketchPlane" : qUnion([Q0])});
            skFitSpline(sketch, "E162", {"points": [v(18.09, 41.3) * mm, v(18.87, 41.04) * mm, v(19.94, 41.11) * mm, v(21.71, 42.77) * mm, v(23.09, 44.33) * mm, v(24.46, 45.54) * mm, v(25.58, 46.06) * mm, v(26.1, 46.23) * mm, v(26.24, 46.14) * mm, v(25.74, 45.83) * mm, v(24.7, 44.97) * mm, v(23.09, 43.08) * mm, v(21.93, 40.35) * mm, v(21.88, 38.41) * mm, v(22.1, 37.2) * mm, v(22.47, 35.2) * mm, v(22.44, 32.82) * mm, v(21.71, 31.09) * mm, v(20.5, 29.07) * mm, v(19.65, 28) * mm, v(19.49, 27.89) * mm, v(19.15, 28.29) * mm, v(19.04, 28.74) * mm, v(19.58, 29.2) * mm, v(20.84, 32.08) * mm, v(21.05, 33.98) * mm, v(20.8, 35.87) * mm, v(20.25, 37.77) * mm, v(19.58, 39.29) * mm, v(18.99, 40.21) * mm, v(18.44, 40.64) * mm, v(18.06, 40.87) * mm, v(17.8, 41.06) * mm, v(17.83, 41.23) * mm, v(18.09, 41.3) * mm]});
            skSolve(sketch);
        }
        {
            var Q0;
            Q0=makeQuery(id+"F92.imprint","IMPRINT",FACE,{"disambiguationData":[TD([[makeQuery(id+"F92.imprint","IMPRINT",EDGE,{"derivedFrom":sQuery(id+"F92.wireOp",EDGE,"E162")}),-1.0]])]});
            extrude(context, id + "F93", {"entities" : qUnion([Q0]), "depth" : 1.83 * mm, "offsetDistance" : 25.4 * mm});
        }
        {
            var Q0;
            Q0=qCreatedBy(makeId("Front.planeOp"),FACE);
            var sketch = newSketch(context, id + "F94", { "sketchPlane" : qUnion([Q0])});
            skFitSpline(sketch, "E163", {"points": [v(18.93, 38.9) * mm, v(19.28, 38.3) * mm, v(19.7, 37.05) * mm, v(19.66, 36.92) * mm, v(19.13, 36.47) * mm, v(18.27, 35.12) * mm, v(17.94, 33.75) * mm, v(17.89, 33.57) * mm, v(17.79, 33.45) * mm, v(17.63, 34.17) * mm, v(17.7, 35.99) * mm, v(18.4, 38.1) * mm, v(18.93, 38.9) * mm]});
            skSolve(sketch);
        }
        {
            var Q0;
            Q0 = qSketchRegion(id + "F94", true);
            extrude(context, id + "F95", {"entities" : qUnion([Q0]), "depth" : 1.83 * mm, "offsetDistance" : 25.4 * mm});
        }
        {
            var Q0;
            Q0=qCreatedBy(makeId("Front.planeOp"),FACE);
            var sketch = newSketch(context, id + "F96", { "sketchPlane" : qUnion([Q0])});
            skFitSpline(sketch, "E164", {"points": [v(1.48, 41.16) * mm, v(2.03, 40.79) * mm, v(3.25, 38.98) * mm, v(3.74, 37.52) * mm, v(3.9, 37.48) * mm, v(4.01, 37.69) * mm, v(4.15, 37.87) * mm, v(4.54, 37.44) * mm, v(5.4, 35.2) * mm, v(6.24, 34.11) * mm, v(9.45, 33.15) * mm, v(11.34, 31.9) * mm, v(11.64, 31.33) * mm, v(11.17, 31.43) * mm, v(9.99, 31.1) * mm, v(8.38, 29.6) * mm, v(7.82, 27.77) * mm, v(7.72, 26.36) * mm, v(7.46, 26.36) * mm, v(7.34, 27.8) * mm, v(7.2, 28.78) * mm, v(6.04, 29.2) * mm, v(4.15, 29.29) * mm, v(2.77, 28.3) * mm, v(2.39, 27.52) * mm, v(2.85, 27.35) * mm, v(3.87, 28.39) * mm, v(4.17, 28.55) * mm, v(3.87, 27.6) * mm, v(3.42, 26.67) * mm, v(3.16, 25.7) * mm, v(2.63, 26) * mm, v(1.47, 26.47) * mm, v(0.26, 26.25) * mm, v(-1.57, 25) * mm, v(-2.9, 23.68) * mm, v(-3.17, 23.55) * mm, v(-2.81, 24.36) * mm, v(-1.4, 26.62) * mm, v(-1.32, 27.4) * mm, v(-2.02, 27.37) * mm, v(-5.15, 26.3) * mm, v(-8.14, 25.35) * mm, v(-8.33, 25.54) * mm, v(-6.6, 26.72) * mm, v(0, 31.12) * mm, v(3.3, 33) * mm, v(3.97, 32.96) * mm, v(8, 32.18) * mm, v(8.9, 32.15) * mm, v(8.96, 32.48) * mm, v(8.8, 32.56) * mm, v(4.13, 33.35) * mm, v(3.2, 33.5) * mm, v(1.9, 32.87) * mm, v(-3.28, 29.63) * mm, v(-3.52, 29.48) * mm, v(-6.9, 29.36) * mm, v(-6.84, 29.61) * mm, v(-5.46, 30.05) * mm, v(-2.5, 31.1) * mm, v(-1.65, 31.8) * mm, v(-1.47, 32.11) * mm, v(-1.88, 32.34) * mm, v(-2.4, 32.26) * mm, v(-2.49, 32.48) * mm, v(-2.24, 32.65) * mm, v(0, 33.23) * mm, v(1.45, 34.25) * mm, v(1.76, 35.38) * mm, v(1.79, 38.67) * mm, v(1.53, 40.22) * mm, v(1.38, 40.87) * mm, v(1.48, 41.16) * mm]});
            skSolve(sketch);
        }
        {
            var Q0;
            Q0 = qSketchRegion(id + "F96", true);
            extrude(context, id + "F97", {"entities" : qUnion([Q0]), "depth" : 1.83 * mm, "offsetDistance" : 25.4 * mm});
        }
        {
            var Q0;
            Q0=qCreatedBy(makeId("Front.planeOp"),FACE);
            var sketch = newSketch(context, id + "F98", { "sketchPlane" : qUnion([Q0])});
            skFitSpline(sketch, "E165", {"points": [v(1.27, 30.72) * mm, v(2.56, 31.16) * mm, v(4.55, 31.32) * mm, v(5.53, 31.32) * mm, v(5.69, 31.44) * mm, v(5.23, 31.58) * mm, v(4.4, 31.66) * mm, v(4.21, 31.98) * mm, v(4.35, 32.22) * mm, v(5.11, 32.24) * mm, v(6.63, 31.96) * mm, v(8.02, 31.56) * mm, v(8.32, 31.08) * mm, v(7.64, 30.68) * mm, v(6.45, 30.54) * mm, v(5.21, 30.5) * mm, v(4.53, 30.48) * mm, v(4.3, 30.48) * mm], "startDerivative": vector(15.42, 6.45) * mm, "endDerivative": vector(-6.63, 0.07) * mm});
            skFitSpline(sketch, "E166", {"points": [v(4.3, 30.48) * mm, v(1.68, 27.93) * mm, v(0.55, 27.03) * mm, v(0, 26.85) * mm, v(-0.29, 27) * mm, v(-0.27, 27.4) * mm, v(1.1, 28.89) * mm, v(1.78, 29.37) * mm, v(2.22, 29.6) * mm, v(2.38, 29.76) * mm, v(2.2, 29.88) * mm, v(1.84, 29.66) * mm, v(0.25, 28.93) * mm, v(-1.64, 28.15) * mm, v(-3.08, 27.77) * mm, v(-3.26, 27.85) * mm, v(-2.66, 28.6) * mm, v(-1.2, 29.52) * mm, v(1.27, 30.72) * mm], "startDerivative": vector(-26.83, -26.87) * mm, "endDerivative": vector(28.71, 13.6) * mm});
            skSolve(sketch);
        }
        {
            var Q0;
            Q0 = qSketchRegion(id + "F98", true);
            extrude(context, id + "F99", {"entities" : qUnion([Q0]), "operationType" : NewBodyOperationType.REMOVE, "depth" : 25.4 * mm, "offsetDistance" : 25.4 * mm});
        }
        {
            var Q0;
            Q0=qCreatedBy(makeId("Front.planeOp"),FACE);
            var sketch = newSketch(context, id + "F100", { "sketchPlane" : qUnion([Q0])});
            skFitSpline(sketch, "E167", {"points": [v(2.4, 34.66) * mm, v(2.37, 36.1) * mm, v(2.49, 37.12) * mm, v(2.79, 37.5) * mm, v(3.28, 36.82) * mm, v(3.37, 35.8) * mm, v(3.21, 34.55) * mm, v(2.94, 34.2) * mm, v(2.59, 34.25) * mm, v(2.4, 34.66) * mm]});
            skSolve(sketch);
        }
        {
            var Q0;
            Q0 = qSketchRegion(id + "F100", true);
            extrude(context, id + "F101", {"entities" : qUnion([Q0]), "operationType" : NewBodyOperationType.REMOVE, "depth" : 25.4 * mm, "offsetDistance" : 25.4 * mm});
        }
        {
            var Q0;
            Q0=qCreatedBy(makeId("Front.planeOp"),FACE);
            var sketch = newSketch(context, id + "F102", { "sketchPlane" : qUnion([Q0])});
            skFitSpline(sketch, "E168", {"points": [v(4.1, 36.03) * mm, v(3.87, 35.76) * mm, v(3.87, 34.71) * mm, v(4.12, 34.13) * mm, v(4.58, 34.18) * mm, v(4.67, 34.7) * mm, v(4.6, 35.35) * mm, v(4.4, 35.78) * mm, v(4.2, 36.04) * mm, v(4.1, 36.03) * mm]});
            skSolve(sketch);
        }
        {
            var Q0;
            Q0 = qSketchRegion(id + "F102", true);
            extrude(context, id + "F103", {"entities" : qUnion([Q0]), "operationType" : NewBodyOperationType.REMOVE, "depth" : 25.4 * mm, "offsetDistance" : 25.4 * mm});
        }
        {
            var Q0;
            Q0=qCreatedBy(makeId("Front.planeOp"),FACE);
            var sketch = newSketch(context, id + "F104", { "sketchPlane" : qUnion([Q0])});
            skFitSpline(sketch, "E169", {"points": [v(18.54, 28.38) * mm, v(19.02, 27.6) * mm, v(20.3, 26.76) * mm, v(21.49, 26.32) * mm, v(21.49, 26.17) * mm, v(20.43, 25.85) * mm, v(15.43, 22.54) * mm, v(12.8, 21.14) * mm, v(11.24, 20.8) * mm, v(11.11, 21) * mm, v(11.04, 21.16) * mm, v(10.77, 21.56) * mm, v(11.05, 21.68) * mm, v(12.32, 21.84) * mm, v(14.97, 23.14) * mm, v(17.8, 26.44) * mm, v(18.38, 27.96) * mm, v(18.38, 28.19) * mm, v(18.42, 28.33) * mm, v(18.48, 28.39) * mm, v(18.54, 28.38) * mm]});
            skSolve(sketch);
        }
        {
            var Q0;
            Q0 = qSketchRegion(id + "F104", true);
            extrude(context, id + "F105", {"entities" : qUnion([Q0]), "depth" : 1.83 * mm, "offsetDistance" : 25.4 * mm});
        }
        {
            var Q0;
            Q0=qCreatedBy(makeId("Front.planeOp"),FACE);
            var sketch = newSketch(context, id + "F106", { "sketchPlane" : qUnion([Q0])});
            skFitSpline(sketch, "E170", {"points": [v(9.96, 22.88) * mm, v(9.93, 22.67) * mm, v(10.4, 22.34) * mm, v(10.62, 22.12) * mm, v(11.72, 22.23) * mm, v(14.92, 23.67) * mm, v(16, 24.7) * mm, v(16.49, 25.17) * mm, v(16.6, 25.48) * mm, v(16.37, 25.42) * mm, v(14.62, 24.1) * mm, v(10.99, 23) * mm, v(10.26, 22.97) * mm, v(9.96, 22.88) * mm]});
            skSolve(sketch);
        }
        {
            var Q0;
            Q0 = qSketchRegion(id + "F106", true);
            extrude(context, id + "F107", {"entities" : qUnion([Q0]), "depth" : 1.83 * mm, "offsetDistance" : 25.4 * mm});
        }
        {
            var Q0;
            Q0=qCreatedBy(makeId("Front.planeOp"),FACE);
            var sketch = newSketch(context, id + "F108", { "sketchPlane" : qUnion([Q0])});
            skFitSpline(sketch, "E171", {"points": [v(19.49, 24.24) * mm, v(19.68, 24.41) * mm, v(19.58, 24.55) * mm, v(19.07, 24.4) * mm, v(18.27, 23.84) * mm, v(15.92, 22.3) * mm, v(13.78, 20.88) * mm, v(12.6, 20.26) * mm, v(12.44, 20.19) * mm, v(11.8, 20.1) * mm, v(11.54, 20.07) * mm, v(11.57, 19.74) * mm, v(11.68, 19.54) * mm, v(11.67, 18.84) * mm, v(11.64, 18.47) * mm, v(11.68, 18.33) * mm, v(11.86, 18.16) * mm, v(12.1, 17.61) * mm, v(12.26, 17.1) * mm, v(12.29, 16.74) * mm, v(12.37, 16.63) * mm, v(12.43, 16.85) * mm, v(12.65, 17.9) * mm, v(12.86, 18.67) * mm, v(14.18, 20.56) * mm, v(16.32, 22.2) * mm, v(19.49, 24.24) * mm]});
            skSolve(sketch);
        }
        {
            var Q0;
            Q0 = qSketchRegion(id + "F108", true);
            extrude(context, id + "F109", {"entities" : qUnion([Q0]), "depth" : 1.83 * mm, "offsetDistance" : 25.4 * mm});
        }
        {
            var Q0;
            Q0=qCreatedBy(makeId("Front.planeOp"),FACE);
            var sketch = newSketch(context, id + "F110", { "sketchPlane" : qUnion([Q0])});
            skFitSpline(sketch, "E172", {"points": [v(-0.3, 21.5) * mm, v(-0.2, 22.73) * mm, v(0.39, 25.26) * mm, v(0.74, 25.74) * mm, v(1.81, 25.69) * mm, v(2.69, 25.05) * mm, v(2.9, 24.6) * mm, v(3, 23.89) * mm, v(3, 23.53) * mm, v(2.5, 24.35) * mm, v(1.74, 24.86) * mm, v(1.01, 24.63) * mm, v(0.49, 24.01) * mm, v(0.13, 23) * mm, v(0, 22.33) * mm, v(-0.16, 21.47) * mm, v(-0.28, 21.35) * mm, v(-0.3, 21.5) * mm]});
            skSolve(sketch);
        }
        {
            var Q0;
            Q0=makeQuery(id+"F110.imprint","IMPRINT",FACE,{"disambiguationData":[TD([[makeQuery(id+"F110.imprint","IMPRINT",EDGE,{"derivedFrom":sQuery(id+"F110.wireOp",EDGE,"E172")}),-1.0]])]});
            extrude(context, id + "F111", {"entities" : qUnion([Q0]), "depth" : 1.83 * mm, "offsetDistance" : 25.4 * mm});
        }
        {
            var Q0;
            Q0=qCreatedBy(makeId("Front.planeOp"),FACE);
            var sketch = newSketch(context, id + "F112", { "sketchPlane" : qUnion([Q0])});
            skFitSpline(sketch, "E173", {"points": [v(5.39, 28.52) * mm, v(4.98, 28.06) * mm, v(3.81, 24.99) * mm, v(3.78, 23.44) * mm, v(3.88, 23.57) * mm, v(4.08, 24.31) * mm, v(4.7, 24.7) * mm, v(5.26, 24.53) * mm, v(5.75, 24) * mm, v(5.87, 23.46) * mm, v(5.84, 23.2) * mm, v(5.45, 23.21) * mm, v(5.2, 23.3) * mm, v(4.98, 23.18) * mm, v(5.6, 22.62) * mm, v(6.7, 21.97) * mm, v(6.95, 21.91) * mm, v(7.03, 22.16) * mm, v(6.78, 22.62) * mm, v(5.7, 25.4) * mm, v(5.53, 26.97) * mm, v(5.58, 28.21) * mm, v(5.56, 28.45) * mm, v(5.55, 28.52) * mm, v(5.46, 28.57) * mm, v(5.39, 28.52) * mm]});
            skSolve(sketch);
        }
        {
            var Q0;
            Q0 = qSketchRegion(id + "F112", true);
            extrude(context, id + "F113", {"entities" : qUnion([Q0]), "depth" : 1.83 * mm, "offsetDistance" : 25.4 * mm});
        }
        {
            var Q0;
            Q0=qCreatedBy(makeId("Front.planeOp"),FACE);
            var sketch = newSketch(context, id + "F114", { "sketchPlane" : qUnion([Q0])});
            skFitSpline(sketch, "E174", {"points": [v(6.31, 27.64) * mm, v(6.36, 28) * mm, v(6.4, 28.16) * mm, v(6.46, 28.3) * mm, v(6.6, 28.25) * mm, v(6.66, 28.09) * mm, v(6.67, 27.48) * mm, v(6.76, 26.86) * mm, v(7.39, 25.48) * mm, v(8.04, 24.3) * mm, v(8.43, 24) * mm, v(8.48, 23.87) * mm, v(8.05, 23.19) * mm, v(7.81, 22.8) * mm, v(7.67, 22.6) * mm, v(7.5, 22.63) * mm, v(7.5, 22.85) * mm, v(7.24, 23.5) * mm, v(6.62, 25.12) * mm, v(6.36, 26.17) * mm, v(6.3, 26.96) * mm, v(6.31, 27.64) * mm]});
            skSolve(sketch);
        }
        {
            var Q0;
            Q0=makeQuery(id+"F114.imprint","IMPRINT",FACE,{"disambiguationData":[TD([[makeQuery(id+"F114.imprint","IMPRINT",EDGE,{"derivedFrom":sQuery(id+"F114.wireOp",EDGE,"E174")}),-1.0]])]});
            extrude(context, id + "F115", {"entities" : qUnion([Q0]), "depth" : 1.83 * mm, "offsetDistance" : 25.4 * mm});
        }
        {
            var Q0;
            Q0=qCreatedBy(makeId("Front.planeOp"),FACE);
            var sketch = newSketch(context, id + "F116", { "sketchPlane" : qUnion([Q0])});
            skFitSpline(sketch, "E175", {"points": [v(1.4, 23.84) * mm, v(1.5, 23.3) * mm, v(2.57, 22.5) * mm, v(3.71, 22.27) * mm, v(4.33, 22.69) * mm, v(4.45, 22.9) * mm, v(4.63, 22.79) * mm, v(5.5, 21.87) * mm, v(6.54, 21.43) * mm, v(7.45, 21.55) * mm, v(8.2, 22.37) * mm, v(8.72, 23.14) * mm, v(8.89, 23.24) * mm, v(8.69, 22.55) * mm, v(8.44, 21.57) * mm, v(8.67, 20.95) * mm, v(8.9, 21.23) * mm, v(9.24, 22.14) * mm, v(9.38, 22.5) * mm, v(9.86, 22.14) * mm, v(10.11, 21.92) * mm, v(9.84, 20.5) * mm, v(9.07, 18.62) * mm, v(8.99, 18.52) * mm, v(8.72, 18.83) * mm, v(8.17, 19.66) * mm, v(7.6, 19.74) * mm, v(7.01, 19.3) * mm, v(6.73, 18.18) * mm, v(6.63, 18.13) * mm, v(5.7, 18.92) * mm, v(4.1, 19.94) * mm, v(2.76, 20.54) * mm, v(1.98, 20.9) * mm, v(1.92, 21.13) * mm, v(2.2, 21.26) * mm, v(2.59, 21.05) * mm, v(3.83, 20.46) * mm, v(5.09, 20.1) * mm, v(5.57, 20.07) * mm, v(5.64, 20.34) * mm, v(4.88, 20.91) * mm, v(3.63, 21.53) * mm, v(1.82, 21.87) * mm, v(0.86, 21.83) * mm, v(0.71, 21.83) * mm, v(0.53, 22.27) * mm, v(0.7, 23) * mm, v(0.88, 23.44) * mm, v(1.1, 23.83) * mm, v(1.23, 23.96) * mm, v(1.4, 23.84) * mm]});
            skSolve(sketch);
        }
        {
            var Q0;
            Q0 = qSketchRegion(id + "F116", true);
            extrude(context, id + "F117", {"entities" : qUnion([Q0]), "depth" : 1.83 * mm, "offsetDistance" : 25.4 * mm});
        }
        {
            var Q0;
            Q0=qCreatedBy(makeId("Front.planeOp"),FACE);
            var sketch = newSketch(context, id + "F118", { "sketchPlane" : qUnion([Q0])});
            skFitSpline(sketch, "E176", {"points": [v(10.57, 21.15) * mm, v(10.85, 20.26) * mm, v(11.15, 19.2) * mm, v(11.1, 18.75) * mm, v(10.57, 17.76) * mm, v(9.81, 15.95) * mm, v(9.2, 14.66) * mm, v(8.84, 14.28) * mm, v(8.62, 14.51) * mm, v(7.48, 15.45) * mm, v(5.42, 16.77) * mm, v(3.86, 17.66) * mm, v(3.6, 17.78) * mm, v(3.53, 17.81) * mm, v(3.4, 18.5) * mm, v(3.34, 19.2) * mm, v(3.28, 19.54) * mm, v(3.8, 19.39) * mm, v(5.19, 18.55) * mm, v(6.8, 16.96) * mm, v(8.42, 15.47) * mm, v(8.64, 15.37) * mm, v(9.02, 15.73) * mm, v(9.44, 17.46) * mm, v(9.5, 18.33) * mm, v(9.6, 18.53) * mm, v(10.25, 20.16) * mm, v(10.41, 21.03) * mm, v(10.45, 21.15) * mm, v(10.5, 21.2) * mm, v(10.57, 21.15) * mm]});
            skSolve(sketch);
        }
        {
            var Q0;
            Q0 = qSketchRegion(id + "F118", true);
            extrude(context, id + "F119", {"entities" : qUnion([Q0]), "depth" : 1.83 * mm, "offsetDistance" : 25.4 * mm});
        }
        {
            var Q0;
            Q0=qCreatedBy(makeId("Front.planeOp"),FACE);
            var sketch = newSketch(context, id + "F120", { "sketchPlane" : qUnion([Q0])});
            skFitSpline(sketch, "E177", {"points": [v(7.38, 18.76) * mm, v(7.21, 17.97) * mm, v(7.14, 17.4) * mm, v(7.6, 16.88) * mm, v(8.42, 15.97) * mm, v(8.65, 15.78) * mm, v(8.8, 16.46) * mm, v(9.07, 17.64) * mm, v(8.94, 18.1) * mm, v(8.04, 19.13) * mm, v(7.64, 19.38) * mm, v(7.38, 18.76) * mm]});
            skSolve(sketch);
        }
        {
            var Q0;
            Q0 = qSketchRegion(id + "F120", true);
            extrude(context, id + "F121", {"entities" : qUnion([Q0]), "depth" : 1.83 * mm, "offsetDistance" : 25.4 * mm});
        }
        {
            var Q0;
            Q0=qCreatedBy(makeId("Front.planeOp"),FACE);
            var sketch = newSketch(context, id + "F122", { "sketchPlane" : qUnion([Q0])});
            skFitSpline(sketch, "E178", {"points": [v(8.05, 18.35) * mm, v(7.9, 18.3) * mm, v(7.78, 17.86) * mm, v(7.78, 17.57) * mm, v(8.05, 17) * mm, v(8.32, 16.92) * mm, v(8.53, 17.1) * mm, v(8.58, 17.22) * mm, v(8.57, 17.48) * mm, v(8.42, 17.94) * mm, v(8.22, 18.24) * mm, v(8.05, 18.35) * mm]});
            skSolve(sketch);
        }
        {
            var Q0;
            Q0 = qSketchRegion(id + "F122", true);
            extrude(context, id + "F123", {"entities" : qUnion([Q0]), "operationType" : NewBodyOperationType.REMOVE, "depth" : 25.4 * mm, "offsetDistance" : 25.4 * mm});
        }
        {
            var Q0;
            Q0=qCreatedBy(makeId("Front.planeOp"),FACE);
            var sketch = newSketch(context, id + "F124", { "sketchPlane" : qUnion([Q0])});
            skFitSpline(sketch, "E179", {"points": [v(9.46, 13.9) * mm, v(10.64, 16.35) * mm, v(11.34, 17.66) * mm, v(11.57, 16.95) * mm, v(11.74, 15.41) * mm, v(11.64, 14.2) * mm, v(10.7, 12.5) * mm, v(9.86, 11.02) * mm, v(9.56, 9.75) * mm, v(9.56, 9.71) * mm], "startDerivative": vector(7.34, 14.58) * mm, "endDerivative": vector(0.14, -1.12) * mm});
            skFitSpline(sketch, "E180", {"points": [v(9.56, 9.75) * mm, v(9.46, 13.9) * mm], "startDerivative": vector(-0.1, 4.16) * mm, "endDerivative": vector(-0.1, 4.16) * mm});
            skSolve(sketch);
        }
        {
            var Q0;
            Q0 = qSketchRegion(id + "F124", true);
            extrude(context, id + "F125", {"entities" : qUnion([Q0]), "depth" : 1.83 * mm, "offsetDistance" : 25.4 * mm});
        }
        {
            var Q0;
            Q0=qCreatedBy(makeId("Front.planeOp"),FACE);
            var sketch = newSketch(context, id + "F126", { "sketchPlane" : qUnion([Q0])});
            skFitSpline(sketch, "E181", {"points": [v(3.61, 12.3) * mm, v(3.5, 12.54) * mm, v(3.08, 12.88) * mm, v(2.5, 13.01) * mm, v(1.4, 12.66) * mm, v(0.27, 11.42) * mm, v(-0.54, 9.8) * mm, v(-0.76, 8.15) * mm, v(-0.4, 6.78) * mm, v(0.29, 5.81) * mm, v(1.15, 5.05) * mm, v(1.57, 4.84) * mm, v(1.62, 4.96) * mm, v(1.65, 5.15) * mm, v(1.66, 5.57) * mm, v(1.44, 5.67) * mm, v(0.25, 7.25) * mm, v(0.17, 8.11) * mm, v(0.35, 8.65) * mm, v(0.58, 8.8) * mm, v(1.03, 8.56) * mm, v(1.36, 7.72) * mm, v(1.5, 7.23) * mm, v(1.57, 7.18) * mm, v(1.66, 8.06) * mm, v(1.67, 8.67) * mm, v(1.56, 9.24) * mm, v(1.36, 9.84) * mm, v(1.2, 10.56) * mm, v(1.4, 11.57) * mm, v(2, 12.45) * mm, v(2.64, 12.67) * mm, v(3.23, 12.53) * mm, v(3.4, 12.25) * mm, v(3.5, 12.18) * mm, v(3.6, 12.18) * mm, v(3.61, 12.3) * mm]});
            skSolve(sketch);
        }
        {
            var Q0;
            Q0 = qSketchRegion(id + "F126", true);
            extrude(context, id + "F127", {"entities" : qUnion([Q0]), "depth" : 1.83 * mm, "offsetDistance" : 25.4 * mm});
        }
        {
            var Q0;
            Q0=qCreatedBy(makeId("Front.planeOp"),FACE);
            var sketch = newSketch(context, id + "F128", { "sketchPlane" : qUnion([Q0])});
            skFitSpline(sketch, "E182", {"points": [v(2.66, 11.92) * mm, v(3.2, 11.48) * mm, v(3.37, 11.28) * mm, v(3.42, 10.28) * mm, v(3.44, 8.45) * mm, v(3.42, 8) * mm, v(3.25, 8.1) * mm, v(2.9, 8.79) * mm, v(2.15, 10.55) * mm, v(2.07, 10.74) * mm, v(2.17, 11.14) * mm, v(2.37, 11.7) * mm, v(2.47, 11.85) * mm, v(2.54, 11.92) * mm, v(2.66, 11.92) * mm]});
            skFitSpline(sketch, "E183", {"points": [v(4.3, 11.52) * mm, v(4.91, 11.77) * mm, v(5.26, 11.93) * mm, v(5.28, 11.85) * mm, v(5.62, 11.1) * mm, v(5.61, 10.97) * mm, v(5.23, 9.95) * mm, v(4.53, 8.82) * mm, v(4.16, 8.32) * mm, v(4.05, 8) * mm, v(3.93, 8) * mm, v(4, 8.28) * mm, v(4.05, 8.65) * mm, v(4.1, 9.25) * mm, v(4.2, 11.16) * mm, v(4.3, 11.52) * mm]});
            skFitSpline(sketch, "E184", {"points": [v(4.62, 7.86) * mm, v(5.26, 8.45) * mm, v(5.92, 9.54) * mm, v(6.32, 10.4) * mm, v(6.39, 10.45) * mm, v(6.9, 10.5) * mm, v(7.16, 10.1) * mm, v(7.15, 9.47) * mm, v(7.08, 9.14) * mm, v(6.8, 8.91) * mm, v(5.12, 7.84) * mm, v(4.74, 7.7) * mm, v(4.64, 7.69) * mm, v(4.62, 7.86) * mm]});
            skSolve(sketch);
        }
        {
            var Q0;
            Q0 = qSketchRegion(id + "F128", true);
            extrude(context, id + "F129", {"entities" : qUnion([Q0]), "depth" : 1.83 * mm, "offsetDistance" : 25.4 * mm});
        }
        {
            var Q0;
            Q0=qCreatedBy(makeId("Front.planeOp"),FACE);
            var sketch = newSketch(context, id + "F130", { "sketchPlane" : qUnion([Q0])});
            skFitSpline(sketch, "E185", {"points": [v(0.55, 13.37) * mm, v(1.07, 14.79) * mm, v(2.45, 16.3) * mm, v(3.28, 16.97) * mm, v(5.04, 16) * mm, v(8.74, 13.5) * mm, v(8.81, 13.23) * mm, v(9.12, 8.88) * mm, v(8.67, 6.04) * mm, v(8.4, 3.8) * mm, v(8.5, 1.68) * mm, v(9.27, -0.68) * mm, v(9.9, -1.04) * mm, v(10.25, -0.8) * mm, v(10.6, 0.6) * mm, v(10.42, 2.09) * mm, v(9.86, 3.07) * mm, v(9.84, 3.11) * mm, v(10.06, 3.26) * mm, v(10.5, 2.7) * mm, v(12.16, 1.67) * mm, v(12.65, 0.3) * mm, v(12.8, -2.92) * mm, v(12.33, -6.2) * mm, v(11.9, -9.67) * mm, v(12.45, -13.5) * mm, v(12.93, -14.53) * mm, v(12.93, -14.7) * mm, v(12.6, -15.35) * mm, v(12.41, -15.53) * mm, v(12.35, -15.43) * mm, v(12.29, -15.04) * mm, v(11.63, -12.88) * mm, v(11.42, -10.27) * mm, v(11.36, -8.22) * mm, v(11.28, -7.27) * mm, v(11.18, -7.08) * mm, v(10.95, -7.13) * mm, v(10.33, -9.43) * mm, v(10.31, -13.09) * mm, v(10.89, -15.55) * mm, v(11.7, -17.02) * mm, v(11.7, -17.09) * mm, v(11.44, -17.8) * mm, v(10.84, -18.59) * mm, v(10.74, -18.67) * mm, v(10.5, -18.36) * mm, v(9.3, -15.96) * mm, v(8.7, -11.8) * mm, v(8.95, -8.12) * mm, v(9.34, -5.57) * mm, v(8.6, -0.21) * mm, v(7.61, 2.58) * mm, v(6.73, 4.75) * mm, v(5.95, 5.77) * mm, v(5.92, 5.8) * mm, v(6.56, 6.53) * mm, v(8.15, 8.41) * mm, v(8.37, 10.52) * mm, v(7.42, 12.1) * mm, v(5.24, 13.71) * mm, v(2.83, 14.27) * mm, v(1.33, 13.88) * mm, v(0.55, 13.37) * mm]});
            skSolve(sketch);
        }
        {
            var Q0;
            Q0 = qSketchRegion(id + "F130", true);
            extrude(context, id + "F131", {"entities" : qUnion([Q0]), "depth" : 1.83 * mm, "offsetDistance" : 25.4 * mm});
        }
        {
            var Q0;
            Q0=qCreatedBy(makeId("Front.planeOp"),FACE);
            var sketch = newSketch(context, id + "F132", { "sketchPlane" : qUnion([Q0])});
            skFitSpline(sketch, "E186", {"points": [v(10.28, 9.57) * mm, v(10.28, 9.91) * mm, v(10.6, 10.47) * mm, v(11.4, 11.92) * mm, v(11.87, 12.13) * mm, v(12.15, 11.5) * mm, v(11.77, 9.57) * mm, v(11.01, 7.39) * mm, v(10.8, 6.25) * mm, v(11.25, 4.62) * mm, v(12.29, 3.72) * mm, v(13.47, 4.28) * mm, v(13.67, 5.56) * mm, v(13.22, 6.35) * mm, v(12.7, 6.08) * mm, v(12.57, 5.1) * mm, v(12.53, 4.76) * mm, v(11.98, 5.38) * mm, v(11.5, 6.5) * mm, v(11.74, 7.8) * mm, v(12.08, 8.6) * mm, v(12.22, 8.77) * mm, v(12.53, 7.94) * mm, v(12.74, 7.87) * mm, v(14.16, 6.56) * mm, v(14.5, 5.38) * mm, v(14.43, 3.97) * mm, v(13.98, 3.24) * mm, v(14.36, 1.86) * mm, v(15.1, 1.13) * mm, v(16.3, 0.89) * mm, v(16.47, 0.75) * mm, v(16.1, 0.65) * mm, v(15.06, 0.65) * mm, v(13.98, 1.24) * mm, v(13.4, 2.03) * mm, v(12.64, 2.93) * mm, v(11.22, 3.83) * mm, v(10.53, 4.73) * mm, v(10.18, 5.76) * mm, v(10.5, 7.56) * mm, v(11.08, 9.05) * mm, v(11.4, 9.84) * mm, v(11.25, 10.47) * mm, v(10.6, 10.09) * mm, v(10.28, 9.57) * mm]});
            skSolve(sketch);
        }
        {
            var Q0;
            Q0 = qSketchRegion(id + "F132", true);
            extrude(context, id + "F133", {"entities" : qUnion([Q0]), "depth" : 1.83 * mm, "offsetDistance" : 25.4 * mm});
        }
        {
            var Q0;
            Q0=qCreatedBy(makeId("Front.planeOp"),FACE);
            var sketch = newSketch(context, id + "F134", { "sketchPlane" : qUnion([Q0])});
            skFitSpline(sketch, "E187", {"points": [v(23.8, 3.1) * mm, v(23.46, 4.47) * mm, v(22.73, 5.98) * mm, v(22.41, 6.22) * mm, v(21.37, 6.13) * mm, v(20.5, 5.75) * mm, v(19.67, 5.66) * mm, v(19.01, 5.9) * mm, v(17.97, 5) * mm, v(17.35, 3.96) * mm, v(16.53, 3.72) * mm, v(15.6, 3.86) * mm, v(15.2, 4.1) * mm, v(14.85, 3.61) * mm, v(14.67, 2.67) * mm, v(15.06, 1.74) * mm, v(16.13, 1.42) * mm, v(16.58, 1.65) * mm, v(16.64, 1.71) * mm, v(16.32, 1.86) * mm, v(15.62, 2.34) * mm, v(15.55, 2.9) * mm, v(15.92, 3.18) * mm, v(16.77, 2.92) * mm, v(17.3, 2.4) * mm, v(17.49, 1.22) * mm, v(17.02, 0.33) * mm, v(15.89, -0.24) * mm, v(15.9, -0.28) * mm, v(16.34, -0.3) * mm, v(17.14, -1.39) * mm, v(17.73, -2.29) * mm, v(18.52, -2.48) * mm, v(19.32, -1.76) * mm, v(19.81, -1.24) * mm, v(20.44, -0.56) * mm, v(20.76, 0.34) * mm, v(20.76, 0.46) * mm, v(20.61, 0.53) * mm, v(20.42, 0.21) * mm, v(19.72, -0.47) * mm, v(19.33, -0.75) * mm, v(18.65, -0.82) * mm, v(18.42, -0.59) * mm, v(18.3, -0.12) * mm, v(18.24, 1.1) * mm, v(18.87, 3.47) * mm, v(19.58, 4.62) * mm, v(20.87, 5.05) * mm, v(21.88, 5) * mm, v(23, 3.98) * mm, v(23.6, 3.02) * mm, v(23.72, 2.95) * mm, v(23.8, 3.1) * mm]});
            skSolve(sketch);
        }
        {
            var Q0;
            Q0 = qSketchRegion(id + "F134", true);
            extrude(context, id + "F135", {"entities" : qUnion([Q0]), "depth" : 1.83 * mm, "offsetDistance" : 25.4 * mm});
        }
        {
            var Q0;
            Q0=qCreatedBy(makeId("Front.planeOp"),FACE);
            var sketch = newSketch(context, id + "F136", { "sketchPlane" : qUnion([Q0])});
            skFitSpline(sketch, "E188", {"points": [v(2.48, 8.12) * mm, v(2.71, 7.82) * mm, v(3.02, 7.25) * mm, v(2.95, 7.12) * mm, v(2.7, 6.29) * mm, v(2.71, 5.78) * mm, v(2.96, 5.88) * mm, v(3.38, 6.68) * mm, v(3.64, 7.16) * mm, v(3.86, 7.25) * mm, v(3.83, 7.07) * mm, v(3.63, 6.1) * mm, v(3.59, 5.37) * mm, v(3.76, 5.16) * mm, v(3.85, 5.21) * mm, v(4.18, 5.9) * mm, v(4.7, 6.97) * mm, v(4.97, 7.04) * mm, v(5.45, 7.3) * mm, v(5.5, 7.15) * mm, v(5.01, 6.71) * mm, v(4.5, 5.68) * mm, v(4.26, 4.56) * mm, v(4.2, 4.43) * mm, v(3, 3.38) * mm, v(2.92, 3.35) * mm, v(2.3, 4.22) * mm, v(2.32, 4.28) * mm, v(2.28, 5.9) * mm, v(2.4, 7.02) * mm, v(2.48, 8.12) * mm]});
            skSolve(sketch);
        }
        {
            var Q0;
            Q0 = qSketchRegion(id + "F136", true);
            extrude(context, id + "F137", {"entities" : qUnion([Q0]), "depth" : 1.83 * mm, "offsetDistance" : 25.4 * mm});
        }
        {
            var Q0;
            Q0=qCreatedBy(makeId("Front.planeOp"),FACE);
            var sketch = newSketch(context, id + "F138", { "sketchPlane" : qUnion([Q0])});
            skFitSpline(sketch, "E189", {"points": [v(-0.42, 5.38) * mm, v(-0.16, 5.1) * mm, v(-0.17, 4.98) * mm, v(-0.57, 4.51) * mm, v(-1.75, 2.85) * mm, v(-3.07, 1.13) * mm, v(-5.85, -2.22) * mm, v(-9.39, -5.38) * mm, v(-12.88, -7.52) * mm, v(-15.47, -8.14) * mm, v(-17.61, -8.01) * mm, v(-19.26, -6.9) * mm, v(-19.83, -5.13) * mm, v(-19.13, -2.8) * mm, v(-17.16, -0.98) * mm, v(-16.75, -0.82) * mm, v(-16.62, -1.27) * mm, v(-15.76, -1.89) * mm, v(-14.65, -2.05) * mm, v(-15.47, -2.5) * mm, v(-17.04, -3.86) * mm, v(-17.6, -4.44) * mm, v(-17.73, -4.35) * mm, v(-17.32, -3.53) * mm, v(-17.57, -2.83) * mm, v(-18.52, -3.24) * mm, v(-19.05, -4.6) * mm, v(-18.98, -5.8) * mm, v(-17.88, -6.55) * mm, v(-16.17, -6.45) * mm, v(-12.3, -5.01) * mm, v(-6.76, -1.6) * mm, v(-3.47, 1.44) * mm, v(-1.74, 3.66) * mm, v(-0.75, 5.1) * mm, v(-0.42, 5.38) * mm]});
            skSolve(sketch);
        }
        {
            var Q0;
            Q0 = qSketchRegion(id + "F138", true);
            extrude(context, id + "F139", {"entities" : qUnion([Q0]), "depth" : 1.83 * mm, "offsetDistance" : 25.4 * mm});
        }
        {
            var Q0;
            Q0=qCreatedBy(makeId("Front.planeOp"),FACE);
            var sketch = newSketch(context, id + "F140", { "sketchPlane" : qUnion([Q0])});
            skFitSpline(sketch, "E190", {"points": [v(0.63, 4.44) * mm, v(1.16, 4.09) * mm, v(1.49, 3.8) * mm, v(1.49, 3.53) * mm, v(2.04, 2.56) * mm, v(2.8, 2.34) * mm, v(3.44, 2.54) * mm, v(3.57, 2.59) * mm, v(3.63, 2.46) * mm, v(3.38, 1.74) * mm, v(2.48, -0.58) * mm, v(0.85, -3.07) * mm, v(-3.72, -7.05) * mm, v(-7.7, -9.85) * mm, v(-7.84, -9.82) * mm, v(-7.9, -9.72) * mm, v(-7.71, -9.5) * mm, v(-7.05, -9.03) * mm, v(-4.83, -7.29) * mm, v(-1.34, -3.4) * mm, v(-0.31, -0.83) * mm, v(-0.3, -0.42) * mm, v(-0.6, -0.27) * mm, v(-1.9, -0.91) * mm, v(-5.4, -4.08) * mm, v(-6.67, -5.89) * mm, v(-7.08, -6.46) * mm, v(-9.48, -9.11) * mm, v(-11.5, -11.97) * mm, v(-13.41, -16.57) * mm, v(-13.69, -19.82) * mm, v(-13.48, -22.52) * mm, v(-11.13, -25.97) * mm, v(-5.8, -28.32) * mm, v(3.6, -26.94) * mm, v(10.86, -22.1) * mm, v(16.11, -14.36) * mm, v(16.8, -13.6) * mm, v(17.08, -14.01) * mm, v(17.08, -15.53) * mm, v(16.04, -19.2) * mm, v(14.66, -22.17) * mm, v(14.18, -23) * mm, v(14.25, -23.2) * mm, v(16.25, -21.27) * mm, v(18.33, -16.5) * mm, v(18.53, -14.22) * mm, v(17.77, -12.21) * mm, v(16.46, -12.21) * mm, v(15.35, -13.8) * mm, v(12.93, -18.3) * mm, v(10.3, -21.55) * mm, v(9.76, -21.84) * mm, v(9.77, -21.65) * mm, v(10.47, -20.6) * mm, v(12.25, -17.88) * mm, v(13.37, -15.2) * mm, v(14.48, -10.08) * mm, v(14.34, -7.47) * mm, v(14.49, -7.3) * mm, v(15.27, -8.03) * mm, v(19.56, -12.35) * mm, v(21.16, -13.92) * mm, v(21.16, -14.13) * mm, v(19.9, -17.18) * mm, v(16.77, -22.07) * mm, v(12.14, -26.28) * mm, v(7.86, -28.98) * mm, v(3.12, -30.7) * mm, v(-2.15, -31.7) * mm, v(-7.56, -31.61) * mm, v(-11.08, -30.77) * mm, v(-14.77, -28.36) * mm, v(-16.3, -25.42) * mm, v(-17.18, -22.1) * mm, v(-17.12, -20.94) * mm, v(-16.98, -21.38) * mm, v(-15.26, -24.72) * mm, v(-12.8, -27.63) * mm, v(-8.6, -29.6) * mm, v(-3.7, -30.28) * mm, v(3.8, -29.03) * mm, v(9.6, -26.2) * mm, v(13.5, -22.16) * mm, v(14.89, -19.75) * mm, v(15.06, -18.97) * mm, v(15, -18.8) * mm, v(14.42, -19.23) * mm, v(12.12, -22.05) * mm, v(10, -24.4) * mm, v(5.3, -27.34) * mm, v(1.4, -28.7) * mm, v(-2.85, -29.46) * mm, v(-8.26, -28.94) * mm, v(-14.27, -24.96) * mm, v(-16.4, -20.86) * mm, v(-16.48, -18.27) * mm, v(-15.76, -15.62) * mm, v(-10.87, -8.83) * mm, v(-6.86, -4.72) * mm, v(-5.96, -3.44) * mm, v(-1.15, 2.1) * mm, v(0.63, 4.44) * mm]});
            skSolve(sketch);
        }
        {
            var Q0;
            Q0 = qSketchRegion(id + "F140", true);
            extrude(context, id + "F141", {"entities" : qUnion([Q0]), "depth" : 1.83 * mm, "offsetDistance" : 25.4 * mm});
        }
        {
            var Q0;
            Q0=qCreatedBy(makeId("Front.planeOp"),FACE);
            var sketch = newSketch(context, id + "F142", { "sketchPlane" : qUnion([Q0])});
            skFitSpline(sketch, "E191", {"points": [v(5.49, 4.48) * mm, v(6.42, 2.27) * mm, v(7.4, -1.33) * mm, v(7.4, -1.74) * mm, v(7.12, -1.5) * mm, v(6.77, -0.52) * mm, v(6.19, 0) * mm, v(4.8, -0.93) * mm, v(3.63, -4.13) * mm, v(2.47, -9.82) * mm, v(1.88, -12.67) * mm, v(0, -16.86) * mm, v(-2.36, -19.83) * mm, v(-2.54, -20.47) * mm, v(-2.13, -20.81) * mm, v(0, -20.23) * mm, v(2.87, -17.15) * mm, v(4.1, -13.14) * mm, v(4.15, -9.24) * mm, v(4.56, -4.47) * mm, v(5.49, -1.92) * mm, v(6.01, -1.16) * mm, v(6.19, -1.04) * mm, v(6.65, -2.2) * mm, v(7.76, -3.31) * mm, v(7.06, -3.84) * mm, v(5.6, -7.1) * mm, v(5.43, -11.45) * mm, v(4.68, -15.06) * mm, v(3.57, -18.55) * mm, v(0, -21.98) * mm, v(-4.51, -22.27) * mm, v(-7.13, -20.17) * mm, v(-7.3, -16.74) * mm, v(-5.73, -13.26) * mm, v(-4.8, -12.27) * mm, v(-4.63, -12.62) * mm, v(-4.63, -13.72) * mm, v(-2.77, -15.99) * mm, v(-1.31, -15.81) * mm, v(-1.2, -15.99) * mm, v(-2.6, -17.67) * mm, v(-3.17, -17.85) * mm, v(-3.52, -16.74) * mm, v(-4.69, -15.52) * mm, v(-5.8, -16.22) * mm, v(-5.56, -18.02) * mm, v(-4.8, -19.19) * mm, v(-3.06, -19.01) * mm, v(-1.14, -17.1) * mm, v(0.84, -13.43) * mm, v(1.36, -8.2) * mm, v(2.3, -3.84) * mm, v(4.1, 0.82) * mm, v(5.49, 4.48) * mm]});
            skSolve(sketch);
        }
        {
            var Q0;
            Q0 = qSketchRegion(id + "F142", true);
            extrude(context, id + "F143", {"entities" : qUnion([Q0]), "depth" : 1.83 * mm, "offsetDistance" : 25.4 * mm});
        }
        {
            var Q0;
            Q0=qCreatedBy(makeId("Front.planeOp"),FACE);
            var sketch = newSketch(context, id + "F144", { "sketchPlane" : qUnion([Q0])});
            skFitSpline(sketch, "E192", {"points": [v(13.51, -1.63) * mm, v(13.77, -2.5) * mm, v(13.75, -4.42) * mm, v(13.6, -5.03) * mm, v(13.9, -5.35) * mm, v(17.09, -8.7) * mm, v(17.7, -9.27) * mm, v(18.05, -8.78) * mm, v(19.27, -7.76) * mm, v(20.46, -7.82) * mm, v(20.93, -8.57) * mm, v(20.81, -9.5) * mm, v(20, -10.26) * mm, v(18.83, -10.2) * mm, v(18.75, -10.35) * mm, v(19.36, -11.13) * mm, v(19.53, -11.34) * mm, v(20.87, -10.55) * mm, v(22.03, -10) * mm, v(22.58, -10.06) * mm, v(22.73, -9.91) * mm, v(22.32, -9.33) * mm, v(21.36, -7.1) * mm, v(21.16, -4.68) * mm, v(21.25, -3.6) * mm, v(20.9, -3.63) * mm, v(20.55, -4.47) * mm, v(19.59, -6.34) * mm, v(18.46, -7.06) * mm, v(17.9, -7.2) * mm, v(16.45, -6.34) * mm, v(15.23, -4.94) * mm, v(14.53, -3.69) * mm, v(14.27, -2.9) * mm, v(13.83, -1.68) * mm, v(13.73, -1.57) * mm, v(13.6, -1.49) * mm, v(13.51, -1.63) * mm]});
            skSolve(sketch);
        }
        {
            var Q0;
            Q0 = qSketchRegion(id + "F144", true);
            extrude(context, id + "F145", {"entities" : qUnion([Q0]), "depth" : 1.83 * mm, "offsetDistance" : 25.4 * mm});
        }
        {
            var Q0;
            Q0=qCreatedBy(makeId("Front.planeOp"),FACE);
            var sketch = newSketch(context, id + "F146", { "sketchPlane" : qUnion([Q0])});
            skFitSpline(sketch, "E193", {"points": [v(36.2, 6.66) * mm, v(36.78, 7.1) * mm, v(37.25, 7.44) * mm, v(37.2, 7.76) * mm, v(36.78, 7.56) * mm, v(35.39, 7.44) * mm, v(32.2, 7.88) * mm, v(30.7, 8.6) * mm, v(30.48, 8.57) * mm, v(29.6, 7) * mm, v(28.64, 4.47) * mm, v(28.06, 0) * mm, v(28.12, -2.85) * mm, v(28.6, -13) * mm, v(27.78, -17) * mm, v(25.72, -20.1) * mm, v(22.86, -21.52) * mm, v(20.56, -21.6) * mm, v(19.49, -21.1) * mm, v(18.92, -20.64) * mm, v(18.62, -21.04) * mm, v(18.14, -21.63) * mm, v(18.14, -21.73) * mm, v(18.95, -22.34) * mm, v(21.77, -22.8) * mm, v(25.95, -21.49) * mm, v(27.87, -19.4) * mm, v(29.72, -15) * mm, v(29.82, -9.77) * mm, v(29.4, -5.45) * mm, v(29.75, -0.54) * mm, v(30.29, 0) * mm, v(30.41, -0.59) * mm, v(30.5, -4.4) * mm, v(30.78, -8.48) * mm, v(31.07, -12.3) * mm, v(30.45, -17.16) * mm, v(28.08, -20.84) * mm, v(25.83, -22.65) * mm, v(20.38, -23.7) * mm, v(17.83, -22.58) * mm, v(17.5, -22.46) * mm, v(17.17, -22.87) * mm, v(16.4, -23.7) * mm, v(17.37, -24.34) * mm, v(20.23, -25.2) * mm, v(24.34, -24.8) * mm, v(28.57, -22.28) * mm, v(32.53, -15.39) * mm, v(32.57, -12.62) * mm, v(32.19, -7.71) * mm, v(31.7, -3.32) * mm, v(31.44, 0.87) * mm, v(31.68, 3.42) * mm, v(31.56, 4.29) * mm, v(31.23, 4.5) * mm, v(30.57, 4) * mm, v(29.8, 1.9) * mm, v(29.17, 0.46) * mm, v(29.1, 0) * mm, v(28.85, 1) * mm, v(29.46, 3.46) * mm, v(30.94, 5.73) * mm, v(32.55, 6.18) * mm, v(32.83, 4.99) * mm, v(32.71, 3.71) * mm, v(32.38, 1.86) * mm, v(32.05, 0) * mm, v(32.18, -2.62) * mm, v(32.46, -3.57) * mm, v(32.46, -2.54) * mm, v(33, 1.08) * mm, v(34.23, 3.92) * mm, v(35.5, 5.97) * mm, v(36.2, 6.66) * mm]});
            skSolve(sketch);
        }
        {
            var Q0;
            Q0 = qSketchRegion(id + "F146", true);
            extrude(context, id + "F147", {"entities" : qUnion([Q0]), "depth" : 1.83 * mm, "offsetDistance" : 25.4 * mm});
        }
        {
            var Q0;
            Q0=qCreatedBy(makeId("Front.planeOp"),FACE);
            var sketch = newSketch(context, id + "F148", { "sketchPlane" : qUnion([Q0])});
            skFitSpline(sketch, "E194", {"points": [v(41.39, 22.56) * mm, v(42.18, 20.87) * mm, v(41.39, 18.19) * mm, v(40.64, 16.1) * mm, v(39.7, 15.78) * mm, v(38.56, 15.94) * mm, v(35.27, 17.04) * mm, v(33.84, 17.42) * mm, v(33.24, 18.19) * mm, v(32.26, 17.7) * mm, v(32.91, 14.96) * mm, v(33.73, 11.72) * mm, v(33.79, 10.24) * mm, v(31.53, 11.08) * mm, v(29.36, 12.05) * mm, v(28.82, 12.36) * mm, v(27.58, 10.97) * mm, v(26.3, 9.96) * mm, v(25.44, 10.27) * mm, v(24, 11.24) * mm, v(21.96, 9.92) * mm, v(20.64, 8.68) * mm, v(19.86, 7.63) * mm, v(17.73, 9.38) * mm, v(16.57, 10.66) * mm, v(16.1, 10.62) * mm, v(16.03, 8.33) * mm, v(15.02, 8.18) * mm, v(13.5, 8.49) * mm, v(14.32, 7.56) * mm, v(15.13, 5.89) * mm, v(15.13, 4.88) * mm, v(16.1, 4.38) * mm, v(17.11, 4.8) * mm, v(17.77, 5.85) * mm, v(18.66, 6.63) * mm, v(20.02, 6.63) * mm, v(20.52, 6.35) * mm, v(22.19, 7.17) * mm, v(24.13, 5.66) * mm, v(24.55, 3.49) * mm, v(24.4, 2.48) * mm, v(23.27, 2.2) * mm, v(22.73, 3.18) * mm, v(21.57, 4.42) * mm, v(19.75, 4.03) * mm, v(18.97, 2.25) * mm, v(18.66, 0) * mm, v(18.87, -0.44) * mm, v(19.84, 0) * mm, v(20.3, 0.83) * mm, v(21.28, 0.87) * mm, v(21.24, 0) * mm, v(20.6, -1.52) * mm, v(19.63, -2.17) * mm, v(18.48, -3.28) * mm, v(17.28, -3.04) * mm, v(16.63, -1.94) * mm, v(16.22, -1.02) * mm, v(15.34, -0.7) * mm, v(14.14, 0) * mm, v(13.73, 0.78) * mm, v(13.6, -0.33) * mm, v(14.65, -1.7) * mm, v(15.3, -3.41) * mm, v(16.26, -5.44) * mm, v(17.46, -6.36) * mm, v(19.26, -6.13) * mm, v(19.95, -4.38) * mm, v(20.46, -3.28) * mm, v(21.66, -3.23) * mm, v(21.89, -4.52) * mm, v(21.7, -6.32) * mm, v(22.95, -8.9) * mm, v(23.5, -10.28) * mm, v(22.49, -10.74) * mm, v(20.46, -11.66) * mm, v(20.04, -11.85) * mm, v(20.55, -12.35) * mm, v(21.75, -13.55) * mm, v(21.84, -14.61) * mm, v(20.04, -18.62) * mm, v(19.77, -20.14) * mm, v(20.73, -20.74) * mm, v(24.33, -19.96) * mm, v(27.14, -16.32) * mm, v(27.74, -12.08) * mm, v(27.28, -1.48) * mm, v(27.74, 4.84) * mm, v(29.21, 8.06) * mm, v(30.23, 9.26) * mm, v(30.87, 9.45) * mm, v(31.89, 8.75) * mm, v(34.24, 8.3) * mm, v(36.31, 8.2) * mm, v(37.79, 8.57) * mm, v(38.39, 7.5) * mm, v(37.14, 6.27) * mm, v(35.8, 4.56) * mm, v(34.52, 1.98) * mm, v(33.46, -3.1) * mm, v(33.55, -5.21) * mm, v(32.63, -4.38) * mm, v(32.3, -4.61) * mm, v(33.78, -12.72) * mm, v(32.95, -17.29) * mm, v(30.37, -22.08) * mm, v(25.1, -25.82) * mm, v(22.34, -26.48) * mm, v(19.1, -26.23) * mm, v(17.1, -25.38) * mm, v(15.79, -24.92) * mm, v(14.39, -25.82) * mm, v(12.33, -27.33) * mm, v(3.56, -32.18) * mm, v(-4.44, -33.06) * mm, v(-11.18, -32.35) * mm, v(-15.51, -30.15) * mm, v(-18.46, -25.3) * mm, v(-19.12, -21.46) * mm, v(-18.46, -19.82) * mm, v(-17.91, -19.6) * mm, v(-17.2, -15.05) * mm, v(-15.12, -11.43) * mm, v(-12.38, -9.02) * mm, v(-13.36, -8.64) * mm, v(-17.8, -9.18) * mm, v(-20.16, -7.54) * mm, v(-20.87, -4.96) * mm, v(-20.32, -2.33) * mm, v(-17.97, 0) * mm, v(-16.21, 0) * mm, v(-16.16, -0.63) * mm, v(-15.45, -1.3) * mm, v(-13.97, -1.46) * mm, v(-14.3, -2.6) * mm, v(-15.56, -3.05) * mm, v(-16.76, -4.47) * mm, v(-18.08, -5.24) * mm, v(-18.08, -4.3) * mm, v(-17.84, -3.87) * mm, v(-17.73, -3.43) * mm, v(-18.1, -3.42) * mm, v(-18.57, -3.84) * mm, v(-18.73, -5) * mm, v(-18.4, -5.83) * mm, v(-17.51, -6.05) * mm, v(-15.84, -5.73) * mm, v(-12.08, -4.12) * mm, v(-8.12, -1.56) * mm, v(-5.96, 0.26) * mm, v(-4.37, 1.71) * mm, v(-1.02, 5.86) * mm, v(-1.18, 6.48) * mm, v(-1.87, 6.71) * mm, v(-3.62, 6.13) * mm, v(-5.01, 5.47) * mm, v(-6.64, 5.2) * mm, v(-7.5, 6.36) * mm, v(-8.85, 8.03) * mm, v(-9.16, 8.3) * mm, v(-10.52, 7.02) * mm, v(-11.56, 5.63) * mm, v(-12.76, 5.55) * mm, v(-14.35, 6.25) * mm, v(-17.1, 7.68) * mm, v(-18.23, 8.34) * mm, v(-18.62, 10.59) * mm, v(-18.7, 10.98) * mm, v(-19.9, 10.16) * mm, v(-21.21, 9.27) * mm, v(-22.22, 10.08) * mm, v(-23.34, 11.9) * mm, v(-23.85, 12.53) * mm, v(-25.82, 11.83) * mm, v(-28.27, 10.7) * mm, v(-28.96, 10.74) * mm, v(-28.97, 13.27) * mm, v(-28.43, 16.67) * mm, v(-28.2, 18.15) * mm, v(-28.87, 19.19) * mm, v(-29.08, 19.8) * mm, v(-29.96, 18.7) * mm, v(-30.67, 17.7) * mm, v(-37.8, 15.4) * mm, v(-38.07, 15.57) * mm, v(-38.73, 18.31) * mm, v(-39.6, 20.12) * mm, v(-39.83, 20.72) * mm, v(-38.95, 22.56) * mm, v(-38.35, 23.96) * mm, v(-40.27, 24.12) * mm, v(-44.32, 23.74) * mm, v(-46.08, 23.68) * mm, v(-46.68, 24.72) * mm, v(-47.45, 26.48) * mm, v(-47.5, 27.2) * mm, v(-46.5, 30.11) * mm, v(-46.22, 30.57) * mm, v(-48.85, 30.53) * mm, v(-51.43, 30.07) * mm, v(-52.12, 30.07) * mm, v(-56.59, 33.34) * mm, v(-56.96, 33.8) * mm, v(-54.98, 36.2) * mm, v(-51.47, 38.87) * mm, v(-50.69, 39.47) * mm, v(-53.96, 39.7) * mm, v(-57.79, 39.56) * mm, v(-59.5, 39.2) * mm, v(-61.21, 38.7) * mm, v(-61.52, 38.85) * mm, v(-61.4, 39.97) * mm, v(-60.5, 41.12) * mm, v(-58.4, 42.38) * mm, v(-53.92, 44.44) * mm, v(-50.55, 45.42) * mm, v(-49.35, 45.7) * mm, v(-51.07, 46.1) * mm, v(-56.86, 47.24) * mm, v(-62.99, 48.4) * mm, v(-66.9, 48.95) * mm, v(-68.15, 49.36) * mm, v(-66.3, 50.29) * mm, v(-60.32, 51.67) * mm, v(-54.23, 51.8) * mm, v(-50.78, 51.58) * mm, v(-54.56, 52.77) * mm, v(-59.3, 54.34) * mm, v(-64.9, 55.7) * mm, v(-69.1, 56.35) * mm, v(-70.9, 56.62) * mm, v(-71.45, 56.67) * mm, v(-69.02, 57.93) * mm], "startDerivative": vector(271.67, -379.95) * mm, "endDerivative": vector(578.61, 103.08) * mm});
            skFitSpline(sketch, "E195", {"points": [v(-69.02, 57.93) * mm, v(-63.32, 58.86) * mm, v(-54.25, 58.51) * mm, v(-44.72, 56.24) * mm, v(-41.17, 54.56) * mm, v(-41.87, 55.6) * mm, v(-41.75, 56.07) * mm, v(-37.16, 53.98) * mm, v(-28.2, 47.3) * mm, v(-27.22, 45.84) * mm, v(-27.39, 48.05) * mm, v(-26.7, 48.51) * mm, v(-26.05, 48.51) * mm, v(-25.47, 47.52) * mm, v(-24.48, 45.25) * mm, v(-21.63, 43.22) * mm, v(-18.38, 43.4) * mm, v(-18.2, 44.1) * mm, v(-19.13, 45.66) * mm, v(-19.07, 46.82) * mm, v(-19.13, 47.23) * mm, v(-20.7, 48.05) * mm, v(-21.52, 48.57) * mm, v(-20.88, 49.38) * mm, v(-17.85, 48.98) * mm, v(-15.3, 47) * mm, v(-14.2, 45.02) * mm, v(-12.1, 43.74) * mm, v(-9.48, 43.22) * mm, v(-10.53, 42.12) * mm, v(-12.21, 40.78) * mm, v(-11.57, 38.22) * mm, v(-12.21, 35.02) * mm, v(-13.2, 34.27) * mm, v(-13.67, 34.44) * mm, v(-13.84, 36.18) * mm, v(-14.42, 37.81) * mm, v(-14.95, 36.24) * mm, v(-14.77, 33.57) * mm, v(-13.32, 30.54) * mm, v(-12.85, 30.08) * mm, v(-12.62, 31.18) * mm, v(-11.69, 28.57) * mm, v(-10.88, 26.88) * mm, v(-10.47, 27.23) * mm, v(-9.36, 26.07) * mm, v(-8.67, 25.78) * mm, v(-5.83, 27.67) * mm, v(-4.41, 28.55) * mm, v(-5.93, 28.55) * mm, v(-7.94, 29.03) * mm, v(-7.93, 30) * mm, v(-7.76, 30.26) * mm, v(-4.73, 30.93) * mm, v(-2.3, 31.7) * mm, v(-1.94, 32.01) * mm, v(-2.73, 32.01) * mm, v(-2.99, 32.62) * mm, v(-2.09, 33.2) * mm, v(0.27, 33.9) * mm, v(1.23, 35.39) * mm, v(1.2, 38.7) * mm, v(0.9, 40.85) * mm, v(0.67, 41.5) * mm, v(1.38, 41.8) * mm, v(2.85, 40.85) * mm, v(3.73, 39) * mm, v(3.8, 38.13) * mm, v(4.07, 38.58) * mm, v(4.93, 37.7) * mm, v(5.63, 36.18) * mm, v(6.22, 34.88) * mm, v(8.23, 33.95) * mm, v(11.48, 32.95) * mm, v(12.46, 31.05) * mm, v(12.46, 30.83) * mm, v(12.19, 30.43) * mm, v(11.8, 30.65) * mm, v(11.3, 30.85) * mm, v(9.8, 30.14) * mm, v(8.47, 28.14) * mm, v(8.47, 25.96) * mm, v(8.13, 25.89) * mm, v(7.86, 25.96) * mm, v(8.3, 24.68) * mm, v(8.92, 23.81) * mm, v(8.72, 23.5) * mm, v(9.27, 23.43) * mm, v(9.13, 22.84) * mm, v(9.75, 23.33) * mm, v(11.03, 23.5) * mm, v(13.31, 24.12) * mm, v(15.73, 25.44) * mm, v(16.53, 25.92) * mm, v(16.88, 25.68) * mm, v(17.64, 26.92) * mm, v(18.09, 28.65) * mm, v(18.15, 28.82) * mm], "startDerivative": vector(277.05, 60.3) * mm, "endDerivative": vector(18.6, 35.96) * mm});
            skFitSpline(sketch, "E196", {"points": [v(18.15, 28.82) * mm, v(18.26, 28.92) * mm, v(18.56, 28.88) * mm, v(18.94, 29.05) * mm, v(19.44, 29.44) * mm, v(20.6, 33.3) * mm, v(20.28, 36.18) * mm, v(20.16, 36.47) * mm, v(19.58, 36.47) * mm, v(19.06, 35.69) * mm, v(18.5, 34.06) * mm, v(18.15, 32.8) * mm, v(18, 32.45) * mm, v(17.67, 32.62) * mm, v(17.02, 35.2) * mm, v(17.51, 37.59) * mm, v(18.37, 39.17) * mm, v(18.69, 39.66) * mm, v(18.15, 39.85) * mm, v(17.17, 40.47) * mm, v(17.07, 41.23) * mm, v(17.55, 42) * mm, v(18.9, 41.72) * mm, v(20.66, 42.62) * mm, v(22.94, 45.52) * mm, v(25.16, 46.49) * mm, v(26.47, 46.56) * mm, v(26.78, 46.14) * mm, v(26.37, 45.45) * mm, v(25.09, 44.66) * mm, v(24.67, 44.07) * mm, v(24.95, 43.55) * mm, v(24.43, 42.58) * mm, v(24.08, 40.85) * mm, v(24.22, 40.06) * mm, v(26.4, 40.34) * mm, v(28.58, 42) * mm, v(29.37, 43.14) * mm], "startDerivative": vector(8.4, 14.62) * mm, "endDerivative": vector(22.76, 37.32) * mm});
            skFitSpline(sketch, "E197", {"points": [v(29.37, 43.14) * mm, v(30.01, 44.21) * mm, v(30.74, 45) * mm, v(31.57, 44.95) * mm, v(31.43, 43.68) * mm, v(31.38, 43.14) * mm, v(32.45, 44.21) * mm, v(39.93, 50.37) * mm, v(45.02, 52.77) * mm, v(47.12, 53.11) * mm, v(46.68, 52.18) * mm, v(46.39, 51.74) * mm, v(47.56, 52.27) * mm, v(55.66, 54.53) * mm, v(65.12, 55.23) * mm, v(69.97, 54) * mm, v(71.04, 53.26) * mm, v(71.04, 52.97) * mm, v(70.75, 52.48) * mm, v(69.85, 52.4) * mm, v(66.31, 51.9) * mm, v(57.4, 49.8) * mm, v(55.7, 49.19) * mm, v(58.34, 48.86) * mm, v(63.97, 47.05) * mm, v(67.83, 44.87) * mm, v(68.16, 43.68) * mm, v(68.08, 43.14) * mm, v(67.2, 43.33) * mm, v(65.56, 43.68) * mm, v(65.17, 43.7) * mm, v(62.58, 44.1) * mm, v(56.9, 43.98) * mm, v(53.18, 43.3) * mm, v(52.32, 43.14) * mm, v(51.75, 42.87) * mm, v(54.23, 42.11) * mm, v(57.4, 40.8) * mm, v(61.59, 38.3) * mm, v(63.4, 36.09) * mm, v(63.4, 35.64) * mm, v(62.86, 35.47) * mm, v(61.14, 35.8) * mm, v(57.31, 36.75) * mm, v(53.24, 37.2) * mm, v(55.1, 35.64) * mm, v(57.85, 32.55) * mm, v(57.93, 32.22) * mm, v(52.7, 28.82) * mm, v(52.59, 28.82) * mm, v(47.65, 29.92) * mm], "startDerivative": vector(43.06, 74.07) * mm, "endDerivative": vector(-233.54, 48.77) * mm});
            skFitSpline(sketch, "E198", {"points": [v(47.65, 29.92) * mm, v(49.04, 26.67) * mm, v(49.07, 26.59) * mm, v(47.04, 23.45) * mm, v(46.92, 23.39) * mm, v(41.2, 23.04) * mm, v(41.02, 23.07) * mm, v(41.39, 22.56) * mm], "startDerivative": vector(7.8, -19.58) * mm, "endDerivative": vector(5.39, -7.18) * mm});
            skSolve(sketch);
        }
        {
            var Q0;
            Q0 = qSketchRegion(id + "F148", true);
            extrude(context, id + "F149", {"entities" : qUnion([Q0]), "oppositeDirection" : true, "depth" : 1.83 * mm, "offsetDistance" : 25.4 * mm});
        }
        {
            var Q0;
            Q0=qCreatedBy(makeId("Front.planeOp"),FACE);
            var sketch = newSketch(context, id + "F150", { "sketchPlane" : qUnion([Q0])});
            skFitSpline(sketch, "E199", {"points": [v(-2.2, 26.68) * mm, v(-2.96, 25.43) * mm, v(-3.71, 23.63) * mm, v(-3.54, 22.9) * mm, v(-2.87, 22.76) * mm, v(-2.37, 23.25) * mm, v(-1.21, 24.59) * mm, v(-0.3, 25.08) * mm, v(-0.54, 24.2) * mm, v(-0.77, 22.58) * mm, v(-0.8, 21.27) * mm, v(-1.15, 21.07) * mm, v(-3.13, 21.21) * mm, v(-5.34, 22.52) * mm, v(-7.11, 23.95) * mm, v(-7.78, 24.65) * mm, v(-6.36, 25.17) * mm, v(-3.28, 26.36) * mm, v(-2.2, 26.68) * mm]});
            skSolve(sketch);
        }
        {
            var Q0;
            Q0 = qSketchRegion(id + "F150", true);
            extrude(context, id + "F151", {"entities" : qUnion([Q0]), "operationType" : NewBodyOperationType.REMOVE, "oppositeDirection" : true, "depth" : 25.4 * mm, "offsetDistance" : 25.4 * mm});
        }
        {
            var Q0;
            Q0=qCreatedBy(makeId("Front.planeOp"),FACE);
            var sketch = newSketch(context, id + "F152", { "sketchPlane" : qUnion([Q0])});
            skFitSpline(sketch, "E200", {"points": [v(1.29, -4.15) * mm, v(0.76, -7.76) * mm, v(0.53, -9.91) * mm, v(0.35, -12.46) * mm, v(0, -13.9) * mm, v(-0.7, -14.8) * mm, v(-1.73, -15.2) * mm, v(-3.25, -14.9) * mm, v(-3.93, -13.24) * mm, v(-3.93, -12) * mm, v(-4.45, -11.38) * mm, v(-6.01, -11.97) * mm, v(-7.4, -14.24) * mm, v(-8.2, -17.02) * mm, v(-8.3, -19.9) * mm, v(-6.4, -22.5) * mm, v(-3.15, -23.52) * mm, v(2.48, -21.59) * mm, v(4.87, -18.05) * mm, v(6.06, -12.42) * mm, v(6.3, -7.6) * mm, v(7.17, -4.93) * mm, v(8.11, -3.99) * mm, v(8.48, -4.96) * mm, v(7.92, -8.35) * mm, v(7.86, -12.08) * mm, v(8.55, -16.85) * mm, v(10.07, -19.41) * mm, v(9.38, -20.66) * mm, v(9.17, -22.1) * mm, v(5.44, -24.88) * mm, v(-3.97, -27.36) * mm, v(-11.92, -23.7) * mm, v(-11.85, -14.92) * mm, v(-9.02, -10.15) * mm, v(-7.98, -10.5) * mm, v(-4.94, -8.9) * mm, v(-0.86, -5.58) * mm, v(1.29, -4.15) * mm]});
            skSolve(sketch);
        }
        {
            var Q0;
            Q0 = qSketchRegion(id + "F152", true);
            extrude(context, id + "F153", {"entities" : qUnion([Q0]), "operationType" : NewBodyOperationType.REMOVE, "oppositeDirection" : true, "depth" : 25.4 * mm, "offsetDistance" : 25.4 * mm});
        }
        {
            var Q0;
            Q0=qCreatedBy(makeId("Front.planeOp"),FACE);
            var sketch = newSketch(context, id + "F154", { "sketchPlane" : qUnion([Q0])});
            skFitSpline(sketch, "E201", {"points": [v(-8.47, -10.3) * mm, v(-8.57, -9.94) * mm, v(-7.91, -9.16) * mm, v(-6.9, -8.56) * mm, v(-2.74, -4.72) * mm, v(-1.17, -2.16) * mm, v(-0.73, -0.94) * mm, v(-0.7, -0.7) * mm, v(-1.87, -1.29) * mm, v(-3.87, -2.98) * mm, v(-5.73, -5.13) * mm, v(-6.78, -6.73) * mm, v(-8.23, -8.06) * mm, v(-9.37, -9.6) * mm, v(-9.47, -9.82) * mm, v(-9.82, -10.5) * mm, v(-10.12, -11.14) * mm, v(-10.31, -11.51) * mm, v(-10.43, -11.85) * mm, v(-10.3, -11.76) * mm, v(-9, -10.92) * mm, v(-8.47, -10.3) * mm]});
            skSolve(sketch);
        }
        {
            var Q0;
            Q0 = qSketchRegion(id + "F154", true);
            extrude(context, id + "F155", {"entities" : qUnion([Q0]), "operationType" : NewBodyOperationType.REMOVE, "oppositeDirection" : true, "depth" : 25.4 * mm, "offsetDistance" : 25.4 * mm});
        }
    });
